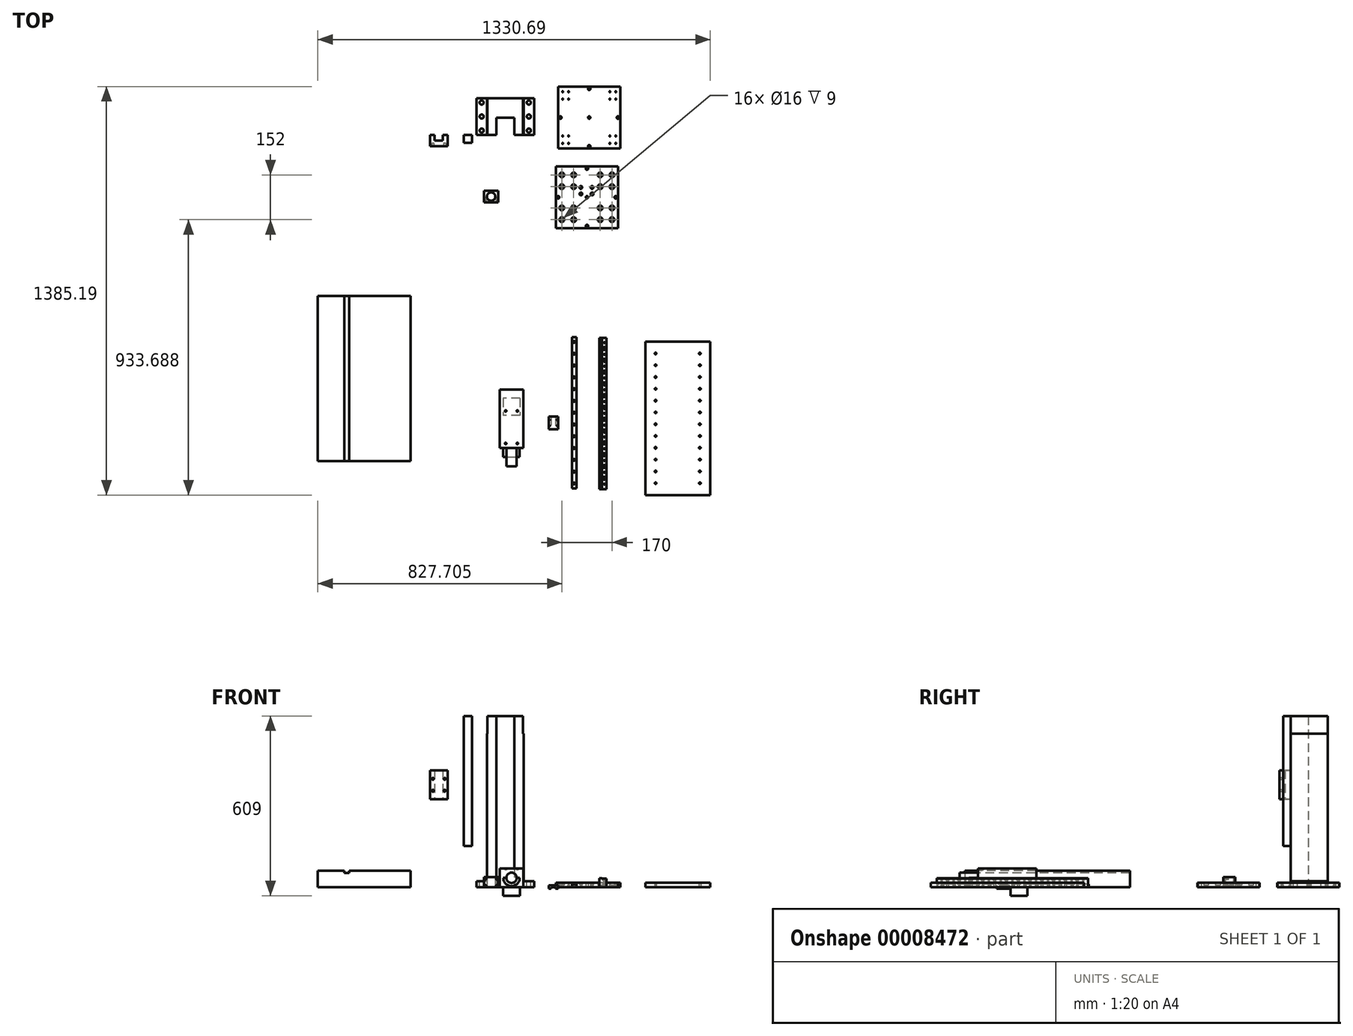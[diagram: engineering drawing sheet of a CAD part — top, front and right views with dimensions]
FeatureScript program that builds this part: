
annotation { "Feature Type Name" : "Feature", "Feature Type Description" : "" }
export const myFeature = defineFeature(function(context is Context, id is Id, definition is map)
    precondition{}
    {
        {
            var Q0;
            Q0=qCreatedBy(makeId("Top.planeOp"),FACE);
            var sketch = newSketch(context, id + "F0", { "sketchPlane" : qUnion([Q0])});
            skLineSegment(sketch, "E0.bottom", {"start": v(-121.15, 80.57) * mm, "end": v(3.85, 80.57) * mm});
            skLineSegment(sketch, "E0.top", {"start": v(-121.15, -44.43) * mm, "end": v(3.85, -44.43) * mm});
            skLineSegment(sketch, "E0.left", {"start": v(-121.15, 80.57) * mm, "end": v(-121.15, -44.43) * mm});
            skLineSegment(sketch, "E0.right", {"start": v(3.85, 80.57) * mm, "end": v(3.85, -44.43) * mm});
            skSolve(sketch);
        }
        {
            var Q0;
            Q0=makeQuery(id+"F0.imprint","IMPRINT",FACE,{"disambiguationData":[TD([[makeQuery(id+"F0.imprint","IMPRINT",EDGE,{"derivedFrom":sQuery(id+"F0.wireOp",EDGE,"E0.bottom")}),-1.0]])]});
            extrude(context, id + "F1", {"entities" : qUnion([Q0]), "depth" : 580 * mm});
        }
        {
            var Q0;
            Q0=makeQuery(id+"F1.opExtrude","SWEPT_FACE",FACE,{"disambiguationData":[OSD([sQuery(id+"F0.wireOp",EDGE,"E0.left")])]});
            var sketch = newSketch(context, id + "F2", { "sketchPlane" : qUnion([Q0])});
            skLineSegment(sketch, "E1.bottom", {"start": v(-80.57, 0) * mm, "end": v(44.43, 0) * mm});
            skLineSegment(sketch, "E1.top", {"start": v(-80.57, 20) * mm, "end": v(44.43, 20) * mm});
            skLineSegment(sketch, "E1.left", {"start": v(-80.57, 0) * mm, "end": v(-80.57, 20) * mm});
            skLineSegment(sketch, "E1.right", {"start": v(44.43, 0) * mm, "end": v(44.43, 20) * mm});
            skSolve(sketch);
        }
        {
            var Q0;
            Q0=makeQuery(id+"F2.imprint","IMPRINT",FACE,{"disambiguationData":[TD([[makeQuery(id+"F2.imprint","IMPRINT",EDGE,{"derivedFrom":sQuery(id+"F2.wireOp",EDGE,"E1.bottom")}),1.0]])]});
            extrude(context, id + "F3", {"entities" : qUnion([Q0]), "operationType" : NewBodyOperationType.ADD, "depth" : 35 * mm});
        }
        {
            var Q0;
            Q0=makeQuery(id+"F1.opExtrude","SWEPT_FACE",FACE,{"disambiguationData":[OSD([sQuery(id+"F0.wireOp",EDGE,"E0.right")])]});
            var sketch = newSketch(context, id + "F4", { "sketchPlane" : qUnion([Q0])});
            skLineSegment(sketch, "E2.bottom", {"start": v(-44.43, 0) * mm, "end": v(80.57, 0) * mm});
            skLineSegment(sketch, "E2.top", {"start": v(-44.43, 20) * mm, "end": v(80.57, 20) * mm});
            skLineSegment(sketch, "E2.left", {"start": v(-44.43, 0) * mm, "end": v(-44.43, 20) * mm});
            skLineSegment(sketch, "E2.right", {"start": v(80.57, 0) * mm, "end": v(80.57, 20) * mm});
            skSolve(sketch);
        }
        {
            var Q0;
            Q0=makeQuery(id+"F4.imprint","IMPRINT",FACE,{"disambiguationData":[TD([[makeQuery(id+"F4.imprint","IMPRINT",EDGE,{"derivedFrom":sQuery(id+"F4.wireOp",EDGE,"E2.bottom")}),-1.0]])]});
            extrude(context, id + "F5", {"entities" : qUnion([Q0]), "operationType" : NewBodyOperationType.ADD, "depth" : 35 * mm});
        }
        {
            var Q0;
            Q0=makeQuery(id+"F5.opExtrude","SWEPT_FACE",FACE,{"disambiguationData":[OSD([sQuery(id+"F4.wireOp",EDGE,"E2.top")])]});
            var sketch = newSketch(context, id + "F6", { "sketchPlane" : qUnion([Q0])});
            skCircle(sketch, "E3", {"center": v(21.35, 65.57) * mm, "radius": 7 * mm});
            skCircle(sketch, "E4", {"center": v(21.35, 18.07) * mm, "radius": 7 * mm});
            skCircle(sketch, "E5", {"center": v(21.35, -29.43) * mm, "radius": 7 * mm});
            skPoint(sketch, "E6", {"position": v(38.85, 18.07) * mm});
            skPoint(sketch, "E7", {"position": v(21.35, 80.57) * mm});
            skSolve(sketch);
        }
        {
            var Q0;
            Q0=makeQuery(id+"F6.imprint","IMPRINT",FACE,{"disambiguationData":[TD([[makeQuery(id+"F6.imprint","IMPRINT",EDGE,{"derivedFrom":sQuery(id+"F6.wireOp",EDGE,"E4")}),1.0]])]});
            var Q1;
            Q1=makeQuery(id+"F6.imprint","IMPRINT",FACE,{"disambiguationData":[TD([[makeQuery(id+"F6.imprint","IMPRINT",EDGE,{"derivedFrom":sQuery(id+"F6.wireOp",EDGE,"E5")}),1.0]])]});
            var Q2;
            Q2=makeQuery(id+"F6.imprint","IMPRINT",FACE,{"disambiguationData":[TD([[makeQuery(id+"F6.imprint","IMPRINT",EDGE,{"derivedFrom":sQuery(id+"F6.wireOp",EDGE,"E3")}),1.0]])]});
            extrude(context, id + "F7", {"entities" : qUnion([Q0, Q1, Q2]), "operationType" : NewBodyOperationType.REMOVE, "oppositeDirection" : true, "depth" : 20 * mm});
        }
        {
            var Q0;
            Q0=makeQuery(id+"F3.opExtrude","SWEPT_FACE",FACE,{"disambiguationData":[OSD([sQuery(id+"F2.wireOp",EDGE,"E1.top")])]});
            var sketch = newSketch(context, id + "F8", { "sketchPlane" : qUnion([Q0])});
            skPoint(sketch, "E8", {"position": v(-138.65, 80.57) * mm});
            skPoint(sketch, "E9", {"position": v(-156.15, 18.07) * mm});
            skCircle(sketch, "E10", {"center": v(-138.65, 65.57) * mm, "radius": 7 * mm});
            skCircle(sketch, "E11", {"center": v(-138.65, 18.07) * mm, "radius": 7 * mm});
            skCircle(sketch, "E12", {"center": v(-138.65, -29.43) * mm, "radius": 7 * mm});
            skSolve(sketch);
        }
        {
            var Q0;
            Q0=makeQuery(id+"F8.imprint","IMPRINT",FACE,{"disambiguationData":[TD([[makeQuery(id+"F8.imprint","IMPRINT",EDGE,{"derivedFrom":sQuery(id+"F8.wireOp",EDGE,"E10")}),1.0]])]});
            var Q1;
            Q1=makeQuery(id+"F8.imprint","IMPRINT",FACE,{"disambiguationData":[TD([[makeQuery(id+"F8.imprint","IMPRINT",EDGE,{"derivedFrom":sQuery(id+"F8.wireOp",EDGE,"E11")}),1.0]])]});
            var Q2;
            Q2=makeQuery(id+"F8.imprint","IMPRINT",FACE,{"disambiguationData":[TD([[makeQuery(id+"F8.imprint","IMPRINT",EDGE,{"derivedFrom":sQuery(id+"F8.wireOp",EDGE,"E12")}),1.0]])]});
            extrude(context, id + "F9", {"entities" : qUnion([Q0, Q1, Q2]), "operationType" : NewBodyOperationType.REMOVE, "oppositeDirection" : true, "depth" : 20 * mm});
        }
        {
            var Q0;
            {var subQ2=sQuery(id+"F2.wireOp",EDGE,"E1.top");Q0=makeQuery(id+"F2.imprint","IMPRINT",FACE,{"disambiguationData":[TD([[makeQuery(id+"F2.imprint","IMPRINT",EDGE,{"derivedFrom":subQ2}),1.0]])]});}
            var sketch = newSketch(context, id + "F10", { "sketchPlane" : qUnion([Q0])});
            skLineSegment(sketch, "E13.bottom", {"start": v(44.43, 580) * mm, "end": v(-80.57, 580) * mm});
            skLineSegment(sketch, "E13.top", {"start": v(44.43, 520) * mm, "end": v(-80.57, 520) * mm});
            skLineSegment(sketch, "E13.left", {"start": v(44.43, 580) * mm, "end": v(44.43, 520) * mm});
            skLineSegment(sketch, "E13.right", {"start": v(-80.57, 580) * mm, "end": v(-80.57, 520) * mm});
            skSolve(sketch);
        }
        {
            var Q0;
            Q0=makeQuery(id+"F10.imprint","IMPRINT",FACE,{"disambiguationData":[TD([[makeQuery(id+"F10.imprint","IMPRINT",EDGE,{"derivedFrom":sQuery(id+"F10.wireOp",EDGE,"E13.bottom")}),-1.0]])]});
            extrude(context, id + "F11", {"entities" : qUnion([Q0]), "operationType" : NewBodyOperationType.REMOVE, "oppositeDirection" : true, "depth" : 2 * mm});
        }
        {
            var Q0;
            {var subQ3=sQuery(id+"F4.wireOp",EDGE,"E2.top");Q0=makeQuery(id+"F4.imprint","IMPRINT",FACE,{"disambiguationData":[TD([[makeQuery(id+"F4.imprint","IMPRINT",EDGE,{"derivedFrom":subQ3}),1.0]])]});}
            var sketch = newSketch(context, id + "F12", { "sketchPlane" : qUnion([Q0])});
            skLineSegment(sketch, "E14.bottom", {"start": v(-44.43, 580) * mm, "end": v(80.57, 580) * mm});
            skLineSegment(sketch, "E14.top", {"start": v(-44.43, 520) * mm, "end": v(80.57, 520) * mm});
            skLineSegment(sketch, "E14.left", {"start": v(-44.43, 580) * mm, "end": v(-44.43, 520) * mm});
            skLineSegment(sketch, "E14.right", {"start": v(80.57, 580) * mm, "end": v(80.57, 520) * mm});
            skLineSegment(sketch, "E15", {"start": v(14.57, 580) * mm, "end": v(14.57, 50.87) * mm});
            skSolve(sketch);
        }
        {
            var Q0;
            Q0=makeQuery(id+"F12.imprint","IMPRINT",FACE,{"disambiguationData":[TD([[makeQuery(id+"F12.imprint","IMPRINT",EDGE,{"derivedFrom":sQuery(id+"F12.wireOp",EDGE,"E14.bottom")}),1.0]])]});
            extrude(context, id + "F13", {"entities" : qUnion([Q0]), "operationType" : NewBodyOperationType.REMOVE, "oppositeDirection" : true, "depth" : 2 * mm});
        }
        {
            var Q0;
            Q0=makeQuery(id+"F5.boolean.opBoolean","MERGE",FACE,{"derivedFrom":[makeQuery(id+"F3.boolean.opBoolean","MERGE",FACE,{"derivedFrom":[makeQuery(id+"F1.opExtrude","SWEPT_FACE",FACE,{"disambiguationData":[OSD([sQuery(id+"F0.wireOp",EDGE,"E0.top")])]}),makeQuery(id+"F3.opExtrude","SWEPT_FACE",FACE,{"disambiguationData":[OSD([sQuery(id+"F2.wireOp",EDGE,"E1.right")])]})]}),makeQuery(id+"F5.opExtrude","SWEPT_FACE",FACE,{"disambiguationData":[OSD([sQuery(id+"F4.wireOp",EDGE,"E2.left")])]})]});
            var sketch = newSketch(context, id + "F14", { "sketchPlane" : qUnion([Q0])});
            skPoint(sketch, "E16", {"position": v(-58.65, 580) * mm});
            skLineSegment(sketch, "E17.bottom", {"start": v(-88.9, 580) * mm, "end": v(-28.4, 580) * mm});
            skLineSegment(sketch, "E17.top", {"start": v(-88.9, 0) * mm, "end": v(-28.4, 0) * mm});
            skLineSegment(sketch, "E17.left", {"start": v(-88.9, 580) * mm, "end": v(-88.9, 0) * mm});
            skLineSegment(sketch, "E17.right", {"start": v(-28.4, 580) * mm, "end": v(-28.4, 0) * mm});
            skSolve(sketch);
        }
        {
            var Q0;
            Q0=makeQuery(id+"F14.imprint","IMPRINT",FACE,{"disambiguationData":[TD([[makeQuery(id+"F14.imprint","IMPRINT",EDGE,{"derivedFrom":sQuery(id+"F14.wireOp",EDGE,"E17.bottom")}),-1.0]])]});
            extrude(context, id + "F15", {"entities" : qUnion([Q0]), "operationType" : NewBodyOperationType.REMOVE, "oppositeDirection" : true, "depth" : 59 * mm});
        }
        {
            var Q0;
            Q0=makeQuery(id+"F5.boolean.opBoolean","MERGE",FACE,{"derivedFrom":[makeQuery(id+"F3.boolean.opBoolean","MERGE",FACE,{"derivedFrom":[makeQuery(id+"F1.opExtrude","SWEPT_FACE",FACE,{"disambiguationData":[OSD([sQuery(id+"F0.wireOp",EDGE,"E0.top")])]}),makeQuery(id+"F3.opExtrude","SWEPT_FACE",FACE,{"disambiguationData":[OSD([sQuery(id+"F2.wireOp",EDGE,"E1.right")])]})]}),makeQuery(id+"F5.opExtrude","SWEPT_FACE",FACE,{"disambiguationData":[OSD([sQuery(id+"F4.wireOp",EDGE,"E2.left")])]})]});
            var sketch = newSketch(context, id + "F16", { "sketchPlane" : qUnion([Q0])});
            skLineSegment(sketch, "E18.bottom", {"start": v(-199.32, 580) * mm, "end": v(-171.32, 580) * mm});
            skLineSegment(sketch, "E18.top", {"start": v(-199.32, 140) * mm, "end": v(-171.32, 140) * mm});
            skLineSegment(sketch, "E18.left", {"start": v(-199.32, 580) * mm, "end": v(-199.32, 140) * mm});
            skLineSegment(sketch, "E18.right", {"start": v(-171.32, 580) * mm, "end": v(-171.32, 140) * mm});
            skPoint(sketch, "E19", {"position": v(-185.32, 580) * mm});
            skPoint(sketch, "E20", {"position": v(-122.53, 0) * mm});
            skLineSegment(sketch, "E21.bottom", {"start": v(-314.15, 396.2) * mm, "end": v(-254.15, 396.2) * mm});
            skLineSegment(sketch, "E21.top", {"start": v(-314.15, 298.2) * mm, "end": v(-254.15, 298.2) * mm});
            skLineSegment(sketch, "E21.left", {"start": v(-314.15, 396.2) * mm, "end": v(-314.15, 298.2) * mm});
            skLineSegment(sketch, "E21.right", {"start": v(-254.15, 396.2) * mm, "end": v(-254.15, 298.2) * mm});
            skPoint(sketch, "E22", {"position": v(-284.15, 298.2) * mm});
            skSolve(sketch);
        }
        {
            var Q0;
            Q0=makeQuery(id+"F16.imprint","IMPRINT",FACE,{"disambiguationData":[TD([[makeQuery(id+"F16.imprint","IMPRINT",EDGE,{"derivedFrom":sQuery(id+"F16.wireOp",EDGE,"E18.bottom")}),-1.0]])]});
            extrude(context, id + "F17", {"entities" : qUnion([Q0]), "depth" : 26 * mm});
        }
        {
            var Q0;
            Q0=makeQuery(id+"F16.imprint","IMPRINT",FACE,{"disambiguationData":[TD([[makeQuery(id+"F16.imprint","IMPRINT",EDGE,{"derivedFrom":sQuery(id+"F16.wireOp",EDGE,"E21.bottom")}),-1.0]])]});
            extrude(context, id + "F18", {"entities" : qUnion([Q0]), "depth" : 38 * mm});
        }
        {
            var Q0;
            Q0=makeQuery(id+"F18.opExtrude","SWEPT_FACE",FACE,{"disambiguationData":[OSD([sQuery(id+"F16.wireOp",EDGE,"E21.top")])]});
            var sketch = newSketch(context, id + "F19", { "sketchPlane" : qUnion([Q0])});
            skLineSegment(sketch, "E23.bottom", {"start": v(-298.15, 44.43) * mm, "end": v(-270.15, 44.43) * mm});
            skLineSegment(sketch, "E23.top", {"start": v(-298.15, 63.43) * mm, "end": v(-270.15, 63.43) * mm});
            skLineSegment(sketch, "E23.left", {"start": v(-298.15, 44.43) * mm, "end": v(-298.15, 63.43) * mm});
            skLineSegment(sketch, "E23.right", {"start": v(-270.15, 44.43) * mm, "end": v(-270.15, 63.43) * mm});
            skPoint(sketch, "E24", {"position": v(-284.15, 44.43) * mm});
            skSolve(sketch);
        }
        {
            var Q0;
            Q0=makeQuery(id+"F19.imprint","IMPRINT",FACE,{"disambiguationData":[TD([[makeQuery(id+"F19.imprint","IMPRINT",EDGE,{"derivedFrom":sQuery(id+"F19.wireOp",EDGE,"E23.bottom")}),1.0]])]});
            extrude(context, id + "F20", {"entities" : qUnion([Q0]), "operationType" : NewBodyOperationType.REMOVE, "oppositeDirection" : true, "depth" : 98 * mm});
        }
        {
            var Q0;
            Q0=makeQuery(id+"F18.opExtrude","CAP_FACE",FACE,{"disambiguationData":[OSD([sQuery(id+"F16.wireOp",EDGE,"E21.bottom"),sQuery(id+"F16.wireOp",EDGE,"E21.top"),sQuery(id+"F16.wireOp",EDGE,"E21.left"),sQuery(id+"F16.wireOp",EDGE,"E21.right")])],"isStart":false});
            var sketch = newSketch(context, id + "F21", { "sketchPlane" : qUnion([Q0])});
            skCircle(sketch, "E25", {"center": v(-304.15, 367.2) * mm, "radius": 3.35 * mm});
            skCircle(sketch, "E26", {"center": v(-304.15, 327.2) * mm, "radius": 3.35 * mm});
            skCircle(sketch, "E27", {"center": v(-264.15, 367.2) * mm, "radius": 3.35 * mm});
            skCircle(sketch, "E28", {"center": v(-264.15, 327.2) * mm, "radius": 3.35 * mm});
            skPoint(sketch, "E29", {"position": v(-284.15, 396.2) * mm});
            skLineSegment(sketch, "E30", {"start": v(-284.15, 396.2) * mm, "end": v(-284.15, 298.2) * mm});
            skPoint(sketch, "E31", {"position": v(-284.15, 347.2) * mm});
            skSolve(sketch);
        }
        {
            var Q0;
            Q0=makeQuery(id+"F21.imprint","IMPRINT",FACE,{"disambiguationData":[TD([[makeQuery(id+"F21.imprint","IMPRINT",EDGE,{"derivedFrom":sQuery(id+"F21.wireOp",EDGE,"E25")}),1.0]])]});
            var Q1;
            Q1=makeQuery(id+"F21.imprint","IMPRINT",FACE,{"disambiguationData":[TD([[makeQuery(id+"F21.imprint","IMPRINT",EDGE,{"derivedFrom":sQuery(id+"F21.wireOp",EDGE,"E26")}),1.0]])]});
            var Q2;
            Q2=makeQuery(id+"F21.imprint","IMPRINT",FACE,{"disambiguationData":[TD([[makeQuery(id+"F21.imprint","IMPRINT",EDGE,{"derivedFrom":sQuery(id+"F21.wireOp",EDGE,"E27")}),1.0]])]});
            var Q3;
            Q3=makeQuery(id+"F21.imprint","IMPRINT",FACE,{"disambiguationData":[TD([[makeQuery(id+"F21.imprint","IMPRINT",EDGE,{"derivedFrom":sQuery(id+"F21.wireOp",EDGE,"E28")}),1.0]])]});
            extrude(context, id + "F22", {"entities" : qUnion([Q0, Q1, Q2, Q3]), "operationType" : NewBodyOperationType.REMOVE, "oppositeDirection" : true, "depth" : 10 * mm});
        }
        {
            var Q0;
            Q0=qCreatedBy(makeId("Top.planeOp"),FACE);
            var sketch = newSketch(context, id + "F23", { "sketchPlane" : qUnion([Q0])});
            skLineSegment(sketch, "E32.bottom", {"start": v(120.9, 119.72) * mm, "end": v(330.9, 119.72) * mm});
            skLineSegment(sketch, "E32.top", {"start": v(120.9, -90.28) * mm, "end": v(330.9, -90.28) * mm});
            skLineSegment(sketch, "E32.left", {"start": v(120.9, 119.72) * mm, "end": v(120.9, -90.28) * mm});
            skLineSegment(sketch, "E32.right", {"start": v(330.9, 119.72) * mm, "end": v(330.9, -90.28) * mm});
            skCircle(sketch, "E33", {"center": v(225.9, 14.72) * mm, "radius": 4 * mm});
            skCircle(sketch, "E34", {"center": v(323.4, 14.72) * mm, "radius": 4.2 * mm});
            skCircle(sketch, "E35", {"center": v(225.9, 112.22) * mm, "radius": 4.2 * mm});
            skCircle(sketch, "E36", {"center": v(128.4, 14.72) * mm, "radius": 4.2 * mm});
            skCircle(sketch, "E37", {"center": v(225.9, -82.78) * mm, "radius": 4.2 * mm});
            skLineSegment(sketch, "E38.bottom", {"start": v(113.2, -150.78) * mm, "end": v(323.2, -150.78) * mm});
            skLineSegment(sketch, "E38.top", {"start": v(113.2, -360.78) * mm, "end": v(323.2, -360.78) * mm});
            skLineSegment(sketch, "E38.left", {"start": v(113.2, -150.78) * mm, "end": v(113.2, -360.78) * mm});
            skLineSegment(sketch, "E38.right", {"start": v(323.2, -150.78) * mm, "end": v(323.2, -360.78) * mm});
            skCircle(sketch, "E39", {"center": v(218.2, -255.78) * mm, "radius": 4 * mm});
            skCircle(sketch, "E40", {"center": v(218.2, -158.28) * mm, "radius": 4.2 * mm});
            skCircle(sketch, "E41", {"center": v(120.7, -255.78) * mm, "radius": 4.2 * mm});
            skCircle(sketch, "E42", {"center": v(315.7, -255.78) * mm, "radius": 4.2 * mm});
            skCircle(sketch, "E43", {"center": v(218.2, -353.28) * mm, "radius": 4.2 * mm});
            skLineSegment(sketch, "E44.bottom", {"start": v(-694.5, -590.16) * mm, "end": v(-379.5, -590.16) * mm});
            skLineSegment(sketch, "E44.top", {"start": v(-694.5, -1150.16) * mm, "end": v(-379.5, -1150.16) * mm});
            skLineSegment(sketch, "E44.left", {"start": v(-694.5, -590.16) * mm, "end": v(-694.5, -1150.16) * mm});
            skLineSegment(sketch, "E44.right", {"start": v(-379.5, -590.16) * mm, "end": v(-379.5, -1150.16) * mm});
            skLineSegment(sketch, "E45.bottom", {"start": v(-130.67, -233.25) * mm, "end": v(-82.67, -233.25) * mm});
            skLineSegment(sketch, "E45.top", {"start": v(-130.67, -273.25) * mm, "end": v(-82.67, -273.25) * mm});
            skLineSegment(sketch, "E45.left", {"start": v(-130.67, -233.25) * mm, "end": v(-130.67, -273.25) * mm});
            skLineSegment(sketch, "E45.right", {"start": v(-82.67, -233.25) * mm, "end": v(-82.67, -273.25) * mm});
            skPoint(sketch, "E46", {"position": v(-106.67, -253.25) * mm});
            skCircle(sketch, "E47", {"center": v(-106.67, -253.25) * mm, "radius": 14 * mm});
            skCircle(sketch, "E48", {"center": v(303.2, -179.78) * mm, "radius": 4.5 * mm});
            skCircle(sketch, "E49", {"center": v(263.2, -179.78) * mm, "radius": 4.5 * mm});
            skCircle(sketch, "E50", {"center": v(263.2, -219.78) * mm, "radius": 4.5 * mm});
            skCircle(sketch, "E51", {"center": v(303.2, -219.78) * mm, "radius": 4.5 * mm});
            skCircle(sketch, "E52", {"center": v(303.2, -331.78) * mm, "radius": 4.5 * mm});
            skCircle(sketch, "E53", {"center": v(303.2, -291.78) * mm, "radius": 4.5 * mm});
            skCircle(sketch, "E54", {"center": v(263.2, -291.78) * mm, "radius": 4.5 * mm});
            skCircle(sketch, "E55", {"center": v(263.2, -331.78) * mm, "radius": 4.5 * mm});
            skCircle(sketch, "E56", {"center": v(173.2, -219.78) * mm, "radius": 4.5 * mm});
            skCircle(sketch, "E57", {"center": v(173.2, -179.78) * mm, "radius": 4.5 * mm});
            skCircle(sketch, "E58", {"center": v(133.2, -179.78) * mm, "radius": 4.5 * mm});
            skCircle(sketch, "E59", {"center": v(133.2, -219.78) * mm, "radius": 4.5 * mm});
            skCircle(sketch, "E60", {"center": v(173.2, -331.78) * mm, "radius": 4.5 * mm});
            skCircle(sketch, "E61", {"center": v(173.2, -291.78) * mm, "radius": 4.5 * mm});
            skCircle(sketch, "E62", {"center": v(133.2, -291.78) * mm, "radius": 4.5 * mm});
            skCircle(sketch, "E63", {"center": v(133.2, -331.78) * mm, "radius": 4.5 * mm});
            skCircle(sketch, "E64", {"center": v(263.2, -179.78) * mm, "radius": 8 * mm});
            skCircle(sketch, "E65", {"center": v(303.2, -179.78) * mm, "radius": 8 * mm});
            skCircle(sketch, "E66", {"center": v(263.2, -219.78) * mm, "radius": 8 * mm});
            skCircle(sketch, "E67", {"center": v(303.2, -219.78) * mm, "radius": 8 * mm});
            skCircle(sketch, "E68", {"center": v(263.2, -291.78) * mm, "radius": 8 * mm});
            skCircle(sketch, "E69", {"center": v(303.2, -291.78) * mm, "radius": 8 * mm});
            skCircle(sketch, "E70", {"center": v(263.2, -331.78) * mm, "radius": 8 * mm});
            skCircle(sketch, "E71", {"center": v(303.2, -331.78) * mm, "radius": 8 * mm});
            skCircle(sketch, "E72", {"center": v(173.2, -179.78) * mm, "radius": 8 * mm});
            skCircle(sketch, "E73", {"center": v(133.2, -179.78) * mm, "radius": 8 * mm});
            skCircle(sketch, "E74", {"center": v(133.2, -219.78) * mm, "radius": 8 * mm});
            skCircle(sketch, "E75", {"center": v(173.2, -219.78) * mm, "radius": 8 * mm});
            skCircle(sketch, "E76", {"center": v(133.2, -291.78) * mm, "radius": 8 * mm});
            skCircle(sketch, "E77", {"center": v(173.2, -291.78) * mm, "radius": 8 * mm});
            skCircle(sketch, "E78", {"center": v(133.2, -331.78) * mm, "radius": 8 * mm});
            skCircle(sketch, "E79", {"center": v(173.2, -331.78) * mm, "radius": 8 * mm});
            skCircle(sketch, "E80", {"center": v(197.7, -222.28) * mm, "radius": 2.65 * mm});
            skCircle(sketch, "E81", {"center": v(235.7, -222.28) * mm, "radius": 2.65 * mm});
            skCircle(sketch, "E82", {"center": v(197.7, -244.28) * mm, "radius": 2.65 * mm});
            skCircle(sketch, "E83", {"center": v(235.7, -244.28) * mm, "radius": 2.65 * mm});
            skCircle(sketch, "E84", {"center": v(197.7, -222.28) * mm, "radius": 4.75 * mm});
            skCircle(sketch, "E85", {"center": v(235.7, -222.28) * mm, "radius": 4.75 * mm});
            skCircle(sketch, "E86", {"center": v(197.7, -244.28) * mm, "radius": 4.75 * mm});
            skCircle(sketch, "E87", {"center": v(235.7, -244.28) * mm, "radius": 4.75 * mm});
            skLineSegment(sketch, "E88.bottom", {"start": v(-77.51, -907.41) * mm, "end": v(2.49, -907.41) * mm});
            skLineSegment(sketch, "E88.top", {"start": v(-77.51, -1105.61) * mm, "end": v(2.49, -1105.61) * mm});
            skLineSegment(sketch, "E88.left", {"start": v(-77.51, -907.41) * mm, "end": v(-77.51, -1105.61) * mm});
            skLineSegment(sketch, "E88.right", {"start": v(2.49, -907.41) * mm, "end": v(2.49, -1105.61) * mm});
            skCircle(sketch, "E89", {"center": v(-57.51, -1090.61) * mm, "radius": 2.68 * mm});
            skCircle(sketch, "E90", {"center": v(-17.51, -1090.61) * mm, "radius": 2.68 * mm});
            skCircle(sketch, "E91", {"center": v(-57.51, -980.61) * mm, "radius": 2.68 * mm});
            skCircle(sketch, "E92", {"center": v(-17.51, -980.61) * mm, "radius": 2.68 * mm});
            skLineSegment(sketch, "E93.bottom", {"start": v(88.31, -999.03) * mm, "end": v(120.31, -999.03) * mm});
            skLineSegment(sketch, "E93.top", {"start": v(88.31, -1042.03) * mm, "end": v(120.31, -1042.03) * mm});
            skLineSegment(sketch, "E93.left", {"start": v(88.31, -999.03) * mm, "end": v(88.31, -1042.03) * mm});
            skLineSegment(sketch, "E93.right", {"start": v(120.31, -999.03) * mm, "end": v(120.31, -1042.03) * mm});
            skLineSegment(sketch, "E94.bottom", {"start": v(167.32, -729.85) * mm, "end": v(182.32, -729.85) * mm});
            skLineSegment(sketch, "E94.top", {"start": v(167.32, -1242.85) * mm, "end": v(182.32, -1242.85) * mm});
            skLineSegment(sketch, "E94.left", {"start": v(167.32, -729.85) * mm, "end": v(167.32, -1242.85) * mm});
            skLineSegment(sketch, "E94.right", {"start": v(182.32, -729.85) * mm, "end": v(182.32, -1242.85) * mm});
            skCircle(sketch, "E95", {"center": v(174.82, -746.35) * mm, "radius": 1.75 * mm});
            skCircle(sketch, "E96", {"center": v(174.82, -786.35) * mm, "radius": 1.75 * mm});
            skCircle(sketch, "E97", {"center": v(174.82, -826.35) * mm, "radius": 1.75 * mm});
            skCircle(sketch, "E98", {"center": v(174.82, -866.35) * mm, "radius": 1.75 * mm});
            skCircle(sketch, "E99", {"center": v(174.82, -906.35) * mm, "radius": 1.75 * mm});
            skCircle(sketch, "E100", {"center": v(174.82, -946.35) * mm, "radius": 1.75 * mm});
            skCircle(sketch, "E101", {"center": v(174.82, -986.35) * mm, "radius": 1.75 * mm});
            skCircle(sketch, "E102", {"center": v(174.82, -1026.35) * mm, "radius": 1.75 * mm});
            skCircle(sketch, "E103", {"center": v(174.82, -1066.35) * mm, "radius": 1.75 * mm});
            skCircle(sketch, "E104", {"center": v(174.82, -1106.35) * mm, "radius": 1.75 * mm});
            skCircle(sketch, "E105", {"center": v(174.82, -1146.35) * mm, "radius": 1.75 * mm});
            skCircle(sketch, "E106", {"center": v(174.82, -1186.35) * mm, "radius": 1.75 * mm});
            skCircle(sketch, "E107", {"center": v(174.82, -1226.35) * mm, "radius": 1.75 * mm});
            skPoint(sketch, "E108", {"position": v(174.82, -729.85) * mm});
            skPoint(sketch, "E109", {"position": v(277.23, -732.27) * mm});
            skLineSegment(sketch, "E110.right", {"start": v(284.73, -732.27) * mm, "end": v(284.73, -1245.27) * mm});
            skLineSegment(sketch, "E110.left", {"start": v(269.73, -732.27) * mm, "end": v(269.73, -1245.27) * mm});
            skCircle(sketch, "E111", {"center": v(277.23, -948.77) * mm, "radius": 1.75 * mm});
            skCircle(sketch, "E112", {"center": v(277.23, -1228.77) * mm, "radius": 1.75 * mm});
            skCircle(sketch, "E113", {"center": v(277.23, -1068.77) * mm, "radius": 1.75 * mm});
            skCircle(sketch, "E114", {"center": v(277.23, -1108.77) * mm, "radius": 1.75 * mm});
            skCircle(sketch, "E115", {"center": v(277.23, -1148.77) * mm, "radius": 1.75 * mm});
            skCircle(sketch, "E116", {"center": v(277.23, -988.77) * mm, "radius": 1.75 * mm});
            skCircle(sketch, "E117", {"center": v(277.23, -908.77) * mm, "radius": 1.75 * mm});
            skCircle(sketch, "E118", {"center": v(277.23, -788.77) * mm, "radius": 1.75 * mm});
            skLineSegment(sketch, "E110.top", {"start": v(269.73, -1245.27) * mm, "end": v(284.73, -1245.27) * mm});
            skCircle(sketch, "E119", {"center": v(277.23, -868.77) * mm, "radius": 1.75 * mm});
            skCircle(sketch, "E120", {"center": v(277.23, -1188.77) * mm, "radius": 1.75 * mm});
            skCircle(sketch, "E121", {"center": v(277.23, -1028.77) * mm, "radius": 1.75 * mm});
            skCircle(sketch, "E122", {"center": v(277.23, -748.77) * mm, "radius": 1.75 * mm});
            skCircle(sketch, "E123", {"center": v(277.23, -828.77) * mm, "radius": 1.75 * mm});
            skLineSegment(sketch, "E110.bottom", {"start": v(269.73, -732.27) * mm, "end": v(284.73, -732.27) * mm});
            skLineSegment(sketch, "E124.bottom", {"start": v(269.73, -732.27) * mm, "end": v(260.23, -732.27) * mm});
            skLineSegment(sketch, "E124.top", {"start": v(269.73, -1245.27) * mm, "end": v(260.23, -1245.27) * mm});
            skLineSegment(sketch, "E124.right", {"start": v(260.23, -732.27) * mm, "end": v(260.23, -1245.27) * mm});
            skCircle(sketch, "E125", {"center": v(277.23, -1208.77) * mm, "radius": 2.8 * mm});
            skCircle(sketch, "E126", {"center": v(277.23, -1168.77) * mm, "radius": 2.8 * mm});
            skCircle(sketch, "E127", {"center": v(277.23, -1128.77) * mm, "radius": 2.8 * mm});
            skCircle(sketch, "E128", {"center": v(277.23, -1088.77) * mm, "radius": 2.8 * mm});
            skCircle(sketch, "E129", {"center": v(277.23, -1048.77) * mm, "radius": 2.8 * mm});
            skCircle(sketch, "E130", {"center": v(277.23, -1008.77) * mm, "radius": 2.8 * mm});
            skCircle(sketch, "E131", {"center": v(277.23, -968.77) * mm, "radius": 2.8 * mm});
            skCircle(sketch, "E132", {"center": v(277.23, -928.77) * mm, "radius": 2.8 * mm});
            skCircle(sketch, "E133", {"center": v(277.23, -888.77) * mm, "radius": 2.8 * mm});
            skCircle(sketch, "E134", {"center": v(277.23, -848.77) * mm, "radius": 2.8 * mm});
            skCircle(sketch, "E135", {"center": v(277.23, -808.77) * mm, "radius": 2.8 * mm});
            skCircle(sketch, "E136", {"center": v(277.23, -768.77) * mm, "radius": 2.8 * mm});
            skLineSegment(sketch, "E137.bottom", {"start": v(416.18, -745.47) * mm, "end": v(636.18, -745.47) * mm});
            skLineSegment(sketch, "E137.top", {"start": v(416.18, -1265.47) * mm, "end": v(636.18, -1265.47) * mm});
            skLineSegment(sketch, "E137.left", {"start": v(416.18, -745.47) * mm, "end": v(416.18, -1265.47) * mm});
            skLineSegment(sketch, "E137.right", {"start": v(636.18, -745.47) * mm, "end": v(636.18, -1265.47) * mm});
            skCircle(sketch, "E138", {"center": v(451.18, -905.47) * mm, "radius": 2.8 * mm});
            skCircle(sketch, "E139", {"center": v(451.18, -865.47) * mm, "radius": 2.8 * mm});
            skCircle(sketch, "E140", {"center": v(451.18, -825.47) * mm, "radius": 2.8 * mm});
            skCircle(sketch, "E141", {"center": v(451.18, -785.47) * mm, "radius": 2.8 * mm});
            skCircle(sketch, "E142", {"center": v(451.18, -1065.47) * mm, "radius": 2.8 * mm});
            skCircle(sketch, "E143", {"center": v(451.18, -1105.47) * mm, "radius": 2.8 * mm});
            skCircle(sketch, "E144", {"center": v(451.18, -1145.47) * mm, "radius": 2.8 * mm});
            skCircle(sketch, "E145", {"center": v(451.18, -1185.47) * mm, "radius": 2.8 * mm});
            skCircle(sketch, "E146", {"center": v(451.18, -1225.47) * mm, "radius": 2.8 * mm});
            skCircle(sketch, "E147", {"center": v(451.18, -945.47) * mm, "radius": 2.8 * mm});
            skCircle(sketch, "E148", {"center": v(451.18, -985.47) * mm, "radius": 2.8 * mm});
            skCircle(sketch, "E149", {"center": v(451.18, -1025.47) * mm, "radius": 2.8 * mm});
            skCircle(sketch, "E150", {"center": v(601.18, -905.47) * mm, "radius": 2.8 * mm});
            skCircle(sketch, "E151", {"center": v(601.18, -865.47) * mm, "radius": 2.8 * mm});
            skCircle(sketch, "E152", {"center": v(601.18, -825.47) * mm, "radius": 2.8 * mm});
            skCircle(sketch, "E153", {"center": v(601.18, -785.47) * mm, "radius": 2.8 * mm});
            skCircle(sketch, "E154", {"center": v(601.18, -1065.47) * mm, "radius": 2.8 * mm});
            skCircle(sketch, "E155", {"center": v(601.18, -1105.47) * mm, "radius": 2.8 * mm});
            skCircle(sketch, "E156", {"center": v(601.18, -1145.47) * mm, "radius": 2.8 * mm});
            skCircle(sketch, "E157", {"center": v(601.18, -1185.47) * mm, "radius": 2.8 * mm});
            skCircle(sketch, "E158", {"center": v(601.18, -1225.47) * mm, "radius": 2.8 * mm});
            skCircle(sketch, "E159", {"center": v(601.18, -945.47) * mm, "radius": 2.8 * mm});
            skCircle(sketch, "E160", {"center": v(601.18, -985.47) * mm, "radius": 2.8 * mm});
            skCircle(sketch, "E161", {"center": v(601.18, -1025.47) * mm, "radius": 2.8 * mm});
            skPoint(sketch, "E162", {"position": v(526.18, -745.47) * mm});
            skCircle(sketch, "E163", {"center": v(135.9, 102.22) * mm, "radius": 1.6 * mm});
            skCircle(sketch, "E164", {"center": v(155.9, 102.22) * mm, "radius": 1.6 * mm});
            skCircle(sketch, "E165", {"center": v(135.9, 77.22) * mm, "radius": 1.6 * mm});
            skCircle(sketch, "E166", {"center": v(155.9, 77.22) * mm, "radius": 1.6 * mm});
            skCircle(sketch, "E167", {"center": v(155.9, 102.22) * mm, "radius": 3 * mm});
            skCircle(sketch, "E168", {"center": v(155.9, 77.22) * mm, "radius": 3 * mm});
            skCircle(sketch, "E169", {"center": v(135.9, 102.22) * mm, "radius": 3 * mm});
            skCircle(sketch, "E170", {"center": v(135.9, 77.22) * mm, "radius": 3 * mm});
            skCircle(sketch, "E171.1.0.0", {"center": v(295.9, 77.22) * mm, "radius": 1.6 * mm});
            skCircle(sketch, "E171.1.0.1", {"center": v(295.9, 102.22) * mm, "radius": 1.6 * mm});
            skCircle(sketch, "E171.1.0.2", {"center": v(295.9, 77.22) * mm, "radius": 3 * mm});
            skCircle(sketch, "E171.1.0.3", {"center": v(315.9, 102.22) * mm, "radius": 1.6 * mm});
            skCircle(sketch, "E171.1.0.4", {"center": v(315.9, 77.22) * mm, "radius": 3 * mm});
            skCircle(sketch, "E171.1.0.5", {"center": v(315.9, 77.22) * mm, "radius": 1.6 * mm});
            skCircle(sketch, "E171.1.0.6", {"center": v(315.9, 102.22) * mm, "radius": 3 * mm});
            skCircle(sketch, "E171.1.0.7", {"center": v(295.9, 102.22) * mm, "radius": 3 * mm});
            skLineSegment(sketch, "E171.direction1", {"start": v(155.9, 77.22) * mm, "end": v(315.9, 77.22) * mm, "construction": true});
            skLineSegment(sketch, "E172.1.0.0", {"start": v(155.9, -72.78) * mm, "end": v(315.9, -72.78) * mm, "construction": true});
            skCircle(sketch, "E172.1.0.1", {"center": v(135.9, -47.78) * mm, "radius": 1.6 * mm});
            skCircle(sketch, "E172.1.0.2", {"center": v(155.9, -47.78) * mm, "radius": 1.6 * mm});
            skCircle(sketch, "E172.1.0.3", {"center": v(315.9, -47.78) * mm, "radius": 3 * mm});
            skCircle(sketch, "E172.1.0.4", {"center": v(295.9, -72.78) * mm, "radius": 3 * mm});
            skCircle(sketch, "E172.1.0.5", {"center": v(295.9, -72.78) * mm, "radius": 1.6 * mm});
            skCircle(sketch, "E172.1.0.6", {"center": v(135.9, -72.78) * mm, "radius": 3 * mm});
            skCircle(sketch, "E172.1.0.7", {"center": v(315.9, -47.78) * mm, "radius": 1.6 * mm});
            skCircle(sketch, "E172.1.0.8", {"center": v(135.9, -47.78) * mm, "radius": 3 * mm});
            skCircle(sketch, "E172.1.0.9", {"center": v(135.9, -72.78) * mm, "radius": 1.6 * mm});
            skCircle(sketch, "E172.1.0.10", {"center": v(155.9, -47.78) * mm, "radius": 3 * mm});
            skCircle(sketch, "E172.1.0.11", {"center": v(315.9, -72.78) * mm, "radius": 3 * mm});
            skCircle(sketch, "E172.1.0.12", {"center": v(295.9, -47.78) * mm, "radius": 3 * mm});
            skCircle(sketch, "E172.1.0.13", {"center": v(295.9, -47.78) * mm, "radius": 1.6 * mm});
            skCircle(sketch, "E172.1.0.14", {"center": v(155.9, -72.78) * mm, "radius": 1.6 * mm});
            skCircle(sketch, "E172.1.0.15", {"center": v(315.9, -72.78) * mm, "radius": 1.6 * mm});
            skCircle(sketch, "E172.1.0.16", {"center": v(155.9, -72.78) * mm, "radius": 3 * mm});
            skLineSegment(sketch, "E172.direction1", {"start": v(155.9, 77.22) * mm, "end": v(155.9, -72.78) * mm, "construction": true});
            skSolve(sketch);
        }
        {
            var Q0;
            Q0=makeQuery(id+"F23.imprint","IMPRINT",FACE,{"disambiguationData":[TD([[makeQuery(id+"F23.imprint","IMPRINT",EDGE,{"derivedFrom":sQuery(id+"F23.wireOp",EDGE,"E32.bottom")}),-1.0]])]});
            extrude(context, id + "F24", {"entities" : qUnion([Q0]), "depth" : 15 * mm});
        }
        {
            var Q0;
            Q0=makeQuery(id+"F23.imprint","IMPRINT",FACE,{"disambiguationData":[TD([[makeQuery(id+"F23.imprint","IMPRINT",EDGE,{"derivedFrom":sQuery(id+"F23.wireOp",EDGE,"E38.bottom")}),-1.0]])]});
            extrude(context, id + "F25", {"entities" : qUnion([Q0]), "depth" : 15 * mm});
        }
        {
            var Q0;
            Q0=makeQuery(id+"F23.imprint","IMPRINT",FACE,{"disambiguationData":[TD([[makeQuery(id+"F23.imprint","IMPRINT",EDGE,{"derivedFrom":sQuery(id+"F23.wireOp",EDGE,"E44.bottom")}),-1.0]])]});
            extrude(context, id + "F27", {"entities" : qUnion([Q0]), "depth" : 55 * mm});
        }
        {
            var Q0;
            Q0=makeQuery(id+"F23.imprint","IMPRINT",FACE,{"disambiguationData":[TD([[makeQuery(id+"F23.imprint","IMPRINT",EDGE,{"derivedFrom":sQuery(id+"F23.wireOp",EDGE,"E45.bottom")}),-1.0]])]});
            extrude(context, id + "F28", {"entities" : qUnion([Q0]), "depth" : 34 * mm});
        }
        {
            var Q0;
            Q0=makeQuery(id+"F27.opExtrude","SWEPT_FACE",FACE,{"disambiguationData":[OSD([sQuery(id+"F23.wireOp",EDGE,"E44.top")])]});
            var sketch = newSketch(context, id + "F29", { "sketchPlane" : qUnion([Q0])});
            skLineSegment(sketch, "E173.bottom", {"start": v(-604.5, 55) * mm, "end": v(-588.5, 55) * mm});
            skLineSegment(sketch, "E173.top", {"start": v(-604.5, 47.5) * mm, "end": v(-588.5, 47.5) * mm});
            skLineSegment(sketch, "E173.left", {"start": v(-604.5, 55) * mm, "end": v(-604.5, 47.5) * mm});
            skLineSegment(sketch, "E173.right", {"start": v(-588.5, 55) * mm, "end": v(-588.5, 47.5) * mm});
            skSolve(sketch);
        }
        {
            var Q0;
            Q0=makeQuery(id+"F29.imprint","IMPRINT",FACE,{"disambiguationData":[TD([[makeQuery(id+"F29.imprint","IMPRINT",EDGE,{"derivedFrom":sQuery(id+"F29.wireOp",EDGE,"E173.bottom")}),-1.0]])]});
            extrude(context, id + "F30", {"entities" : qUnion([Q0]), "operationType" : NewBodyOperationType.REMOVE, "oppositeDirection" : true, "depth" : 560 * mm});
        }
        {
            var Q0;
            Q0=makeQuery(id+"F23.imprint","IMPRINT",FACE,{"disambiguationData":[TD([[makeQuery(id+"F23.imprint","IMPRINT",EDGE,{"derivedFrom":sQuery(id+"F23.wireOp",EDGE,"E55")}),-1.0]])]});
            var Q1;
            Q1=makeQuery(id+"F23.imprint","IMPRINT",FACE,{"disambiguationData":[TD([[makeQuery(id+"F23.imprint","IMPRINT",EDGE,{"derivedFrom":sQuery(id+"F23.wireOp",EDGE,"E54")}),-1.0]])]});
            var Q2;
            Q2=makeQuery(id+"F23.imprint","IMPRINT",FACE,{"disambiguationData":[TD([[makeQuery(id+"F23.imprint","IMPRINT",EDGE,{"derivedFrom":sQuery(id+"F23.wireOp",EDGE,"E53")}),-1.0]])]});
            var Q3;
            Q3=makeQuery(id+"F23.imprint","IMPRINT",FACE,{"disambiguationData":[TD([[makeQuery(id+"F23.imprint","IMPRINT",EDGE,{"derivedFrom":sQuery(id+"F23.wireOp",EDGE,"E52")}),-1.0]])]});
            var Q4;
            Q4=makeQuery(id+"F23.imprint","IMPRINT",FACE,{"disambiguationData":[TD([[makeQuery(id+"F23.imprint","IMPRINT",EDGE,{"derivedFrom":sQuery(id+"F23.wireOp",EDGE,"E50")}),-1.0]])]});
            var Q5;
            Q5=makeQuery(id+"F23.imprint","IMPRINT",FACE,{"disambiguationData":[TD([[makeQuery(id+"F23.imprint","IMPRINT",EDGE,{"derivedFrom":sQuery(id+"F23.wireOp",EDGE,"E51")}),-1.0]])]});
            var Q6;
            Q6=makeQuery(id+"F23.imprint","IMPRINT",FACE,{"disambiguationData":[TD([[makeQuery(id+"F23.imprint","IMPRINT",EDGE,{"derivedFrom":sQuery(id+"F23.wireOp",EDGE,"E49")}),-1.0]])]});
            var Q7;
            Q7=makeQuery(id+"F23.imprint","IMPRINT",FACE,{"disambiguationData":[TD([[makeQuery(id+"F23.imprint","IMPRINT",EDGE,{"derivedFrom":sQuery(id+"F23.wireOp",EDGE,"E48")}),-1.0]])]});
            var Q8;
            Q8=makeQuery(id+"F23.imprint","IMPRINT",FACE,{"disambiguationData":[TD([[makeQuery(id+"F23.imprint","IMPRINT",EDGE,{"derivedFrom":sQuery(id+"F23.wireOp",EDGE,"E58")}),-1.0]])]});
            var Q9;
            Q9=makeQuery(id+"F23.imprint","IMPRINT",FACE,{"disambiguationData":[TD([[makeQuery(id+"F23.imprint","IMPRINT",EDGE,{"derivedFrom":sQuery(id+"F23.wireOp",EDGE,"E57")}),-1.0]])]});
            var Q10;
            Q10=makeQuery(id+"F23.imprint","IMPRINT",FACE,{"disambiguationData":[TD([[makeQuery(id+"F23.imprint","IMPRINT",EDGE,{"derivedFrom":sQuery(id+"F23.wireOp",EDGE,"E59")}),-1.0]])]});
            var Q11;
            Q11=makeQuery(id+"F23.imprint","IMPRINT",FACE,{"disambiguationData":[TD([[makeQuery(id+"F23.imprint","IMPRINT",EDGE,{"derivedFrom":sQuery(id+"F23.wireOp",EDGE,"E56")}),-1.0]])]});
            var Q12;
            Q12=makeQuery(id+"F23.imprint","IMPRINT",FACE,{"disambiguationData":[TD([[makeQuery(id+"F23.imprint","IMPRINT",EDGE,{"derivedFrom":sQuery(id+"F23.wireOp",EDGE,"E62")}),-1.0]])]});
            var Q13;
            Q13=makeQuery(id+"F23.imprint","IMPRINT",FACE,{"disambiguationData":[TD([[makeQuery(id+"F23.imprint","IMPRINT",EDGE,{"derivedFrom":sQuery(id+"F23.wireOp",EDGE,"E61")}),-1.0]])]});
            var Q14;
            Q14=makeQuery(id+"F23.imprint","IMPRINT",FACE,{"disambiguationData":[TD([[makeQuery(id+"F23.imprint","IMPRINT",EDGE,{"derivedFrom":sQuery(id+"F23.wireOp",EDGE,"E63")}),-1.0]])]});
            var Q15;
            Q15=makeQuery(id+"F23.imprint","IMPRINT",FACE,{"disambiguationData":[TD([[makeQuery(id+"F23.imprint","IMPRINT",EDGE,{"derivedFrom":sQuery(id+"F23.wireOp",EDGE,"E60")}),-1.0]])]});
            var Q16;
            Q16=sQuery(id+"F23.wireOp",EDGE,"E70");
            var Q17;
            Q17=sQuery(id+"F23.wireOp",EDGE,"E71");
            var Q18;
            Q18=sQuery(id+"F23.wireOp",EDGE,"E68");
            var Q19;
            Q19=sQuery(id+"F23.wireOp",EDGE,"E69");
            var Q20;
            Q20=sQuery(id+"F23.wireOp",EDGE,"E66");
            var Q21;
            Q21=sQuery(id+"F23.wireOp",EDGE,"E67");
            var Q22;
            Q22=sQuery(id+"F23.wireOp",EDGE,"E64");
            var Q23;
            Q23=sQuery(id+"F23.wireOp",EDGE,"E65");
            extrude(context, id + "F31", {"entities" : qUnion([Q0, Q1, Q2, Q3, Q4, Q5, Q6, Q7, Q8, Q9, Q10, Q11, Q12, Q13, Q14, Q15]), "operationType" : NewBodyOperationType.ADD, "surfaceEntities" : qUnion([Q16, Q17, Q18, Q19, Q20, Q21, Q22, Q23]), "depth" : 6 * mm});
        }
        {
            var Q0;
            Q0=makeQuery(id+"F28.opExtrude","SWEPT_FACE",FACE,{"disambiguationData":[OSD([sQuery(id+"F23.wireOp",EDGE,"E45.top")])]});
            var sketch = newSketch(context, id + "F32", { "sketchPlane" : qUnion([Q0])});
            skCircle(sketch, "E174", {"center": v(-125.67, 27.5) * mm, "radius": 2.02 * mm});
            skCircle(sketch, "E175", {"center": v(-87.67, 27.5) * mm, "radius": 2.02 * mm});
            skCircle(sketch, "E176", {"center": v(-125.67, 5.5) * mm, "radius": 2.02 * mm});
            skCircle(sketch, "E177", {"center": v(-87.67, 5.5) * mm, "radius": 2.02 * mm});
            skSolve(sketch);
        }
        {
            var Q0;
            Q0=makeQuery(id+"F32.imprint","IMPRINT",FACE,{"disambiguationData":[TD([[makeQuery(id+"F32.imprint","IMPRINT",EDGE,{"derivedFrom":sQuery(id+"F32.wireOp",EDGE,"E174")}),1.0]])]});
            var Q1;
            Q1=makeQuery(id+"F32.imprint","IMPRINT",FACE,{"disambiguationData":[TD([[makeQuery(id+"F32.imprint","IMPRINT",EDGE,{"derivedFrom":sQuery(id+"F32.wireOp",EDGE,"E176")}),1.0]])]});
            var Q2;
            Q2=makeQuery(id+"F32.imprint","IMPRINT",FACE,{"disambiguationData":[TD([[makeQuery(id+"F32.imprint","IMPRINT",EDGE,{"derivedFrom":sQuery(id+"F32.wireOp",EDGE,"E177")}),1.0]])]});
            var Q3;
            Q3=makeQuery(id+"F32.imprint","IMPRINT",FACE,{"disambiguationData":[TD([[makeQuery(id+"F32.imprint","IMPRINT",EDGE,{"derivedFrom":sQuery(id+"F32.wireOp",EDGE,"E175")}),1.0]])]});
            extrude(context, id + "F33", {"entities" : qUnion([Q0, Q1, Q2, Q3]), "operationType" : NewBodyOperationType.REMOVE, "oppositeDirection" : true, "depth" : 17 * mm});
        }
        {
            var Q0;
            Q0=makeQuery(id+"F23.imprint","IMPRINT",FACE,{"disambiguationData":[TD([[makeQuery(id+"F23.imprint","IMPRINT",EDGE,{"derivedFrom":sQuery(id+"F23.wireOp",EDGE,"E80")}),-1.0]])]});
            var Q1;
            Q1=makeQuery(id+"F23.imprint","IMPRINT",FACE,{"disambiguationData":[TD([[makeQuery(id+"F23.imprint","IMPRINT",EDGE,{"derivedFrom":sQuery(id+"F23.wireOp",EDGE,"E82")}),-1.0]])]});
            var Q2;
            Q2=makeQuery(id+"F23.imprint","IMPRINT",FACE,{"disambiguationData":[TD([[makeQuery(id+"F23.imprint","IMPRINT",EDGE,{"derivedFrom":sQuery(id+"F23.wireOp",EDGE,"E81")}),-1.0]])]});
            var Q3;
            Q3=makeQuery(id+"F23.imprint","IMPRINT",FACE,{"disambiguationData":[TD([[makeQuery(id+"F23.imprint","IMPRINT",EDGE,{"derivedFrom":sQuery(id+"F23.wireOp",EDGE,"E83")}),-1.0]])]});
            extrude(context, id + "F34", {"entities" : qUnion([Q0, Q1, Q2, Q3]), "operationType" : NewBodyOperationType.ADD, "depth" : 8 * mm});
        }
        {
            var Q0;
            Q0=makeQuery(id+"F23.imprint","IMPRINT",FACE,{"disambiguationData":[TD([[makeQuery(id+"F23.imprint","IMPRINT",EDGE,{"derivedFrom":sQuery(id+"F23.wireOp",EDGE,"E88.bottom")}),-1.0]])]});
            extrude(context, id + "F35", {"entities" : qUnion([Q0]), "depth" : 63 * mm});
        }
        {
            var Q0;
            Q0=makeQuery(id+"F23.imprint","IMPRINT",FACE,{"disambiguationData":[TD([[makeQuery(id+"F23.imprint","IMPRINT",EDGE,{"derivedFrom":sQuery(id+"F23.wireOp",EDGE,"E90")}),1.0]])]});
            var Q1;
            Q1=makeQuery(id+"F23.imprint","IMPRINT",FACE,{"disambiguationData":[TD([[makeQuery(id+"F23.imprint","IMPRINT",EDGE,{"derivedFrom":sQuery(id+"F23.wireOp",EDGE,"E89")}),1.0]])]});
            var Q2;
            Q2=makeQuery(id+"F23.imprint","IMPRINT",FACE,{"disambiguationData":[TD([[makeQuery(id+"F23.imprint","IMPRINT",EDGE,{"derivedFrom":sQuery(id+"F23.wireOp",EDGE,"E92")}),1.0]])]});
            var Q3;
            Q3=makeQuery(id+"F23.imprint","IMPRINT",FACE,{"disambiguationData":[TD([[makeQuery(id+"F23.imprint","IMPRINT",EDGE,{"derivedFrom":sQuery(id+"F23.wireOp",EDGE,"E91")}),1.0]])]});
            extrude(context, id + "F36", {"entities" : qUnion([Q0, Q1, Q2, Q3]), "operationType" : NewBodyOperationType.ADD, "depth" : 58 * mm});
        }
        {
            var Q0;
            Q0=makeQuery(id+"F23.imprint","IMPRINT",FACE,{"disambiguationData":[TD([[makeQuery(id+"F23.imprint","IMPRINT",EDGE,{"derivedFrom":sQuery(id+"F23.wireOp",EDGE,"E88.bottom")}),-1.0]])]});
            var sketch = newSketch(context, id + "F37", { "sketchPlane" : qUnion([Q0])});
            skLineSegment(sketch, "E178.bottom", {"start": v(-8.76, -937.61) * mm, "end": v(-66.26, -937.61) * mm});
            skLineSegment(sketch, "E178.top", {"start": v(-8.76, -995.11) * mm, "end": v(-66.26, -995.11) * mm});
            skLineSegment(sketch, "E178.left", {"start": v(-8.76, -937.61) * mm, "end": v(-8.76, -995.11) * mm});
            skLineSegment(sketch, "E178.right", {"start": v(-66.26, -937.61) * mm, "end": v(-66.26, -995.11) * mm});
            skSolve(sketch);
        }
        {
            var Q0;
            Q0=makeQuery(id+"F37.imprint","IMPRINT",FACE,{"disambiguationData":[TD([[makeQuery(id+"F37.imprint","IMPRINT",EDGE,{"derivedFrom":sQuery(id+"F37.wireOp",EDGE,"E178.bottom")}),1.0]])]});
            extrude(context, id + "F38", {"entities" : qUnion([Q0]), "operationType" : NewBodyOperationType.ADD, "oppositeDirection" : true, "depth" : 29 * mm});
        }
        {
            var Q0;
            Q0=makeQuery(id+"F23.imprint","IMPRINT",FACE,{"disambiguationData":[TD([[makeQuery(id+"F23.imprint","IMPRINT",EDGE,{"derivedFrom":sQuery(id+"F23.wireOp",EDGE,"E91")}),1.0]])]});
            var Q1;
            Q1=makeQuery(id+"F23.imprint","IMPRINT",FACE,{"disambiguationData":[TD([[makeQuery(id+"F23.imprint","IMPRINT",EDGE,{"derivedFrom":sQuery(id+"F23.wireOp",EDGE,"E92")}),1.0]])]});
            extrude(context, id + "F39", {"entities" : qUnion([Q0, Q1]), "operationType" : NewBodyOperationType.ADD, "oppositeDirection" : true, "depth" : 29 * mm});
        }
        {
            var Q0;
            Q0=makeQuery(id+"F35.opExtrude","SWEPT_FACE",FACE,{"disambiguationData":[OSD([sQuery(id+"F23.wireOp",EDGE,"E88.top")])]});
            var sketch = newSketch(context, id + "F40", { "sketchPlane" : qUnion([Q0])});
            skCircle(sketch, "E179", {"center": v(-37.51, 31.5) * mm, "radius": 28 * mm});
            skPoint(sketch, "E180", {"position": v(-77.51, 31.5) * mm});
            skPoint(sketch, "E181", {"position": v(-37.51, 63) * mm});
            skLineSegment(sketch, "E182", {"start": v(-77.51, 31.5) * mm, "end": v(2.49, 31.5) * mm});
            skLineSegment(sketch, "E183", {"start": v(-37.51, 63) * mm, "end": v(-37.51, 0) * mm});
            skCircle(sketch, "E184", {"center": v(-37.51, 31.5) * mm, "radius": 17.5 * mm});
            skSolve(sketch);
        }
        {
            var Q0;
            {var subQ0=sQuery(id+"F40.wireOp",EDGE,"E184");var subQ3=sQuery(id+"F40.wireOp",EDGE,"E182");var subQ4=makeQuery(id+"F40.imprint","INTERSECT",VERTEX,{"disambiguationData":[OD(0.0)],"derivedFrom":[subQ3,subQ0]});Q0=makeQuery(id+"F40.imprint","IMPRINT",FACE,{"disambiguationData":[TD([[makeQuery(id+"F40.imprint","IMPRINT",EDGE,{"disambiguationData":[TD([[subQ4,-1.0]])],"derivedFrom":subQ3}),1.0]])]});}
            var Q1;
            {var subQ1=sQuery(id+"F40.wireOp",EDGE,"E183");var subQ3=sQuery(id+"F40.wireOp",EDGE,"E182");var subQ5=makeQuery(id+"F40.imprint","INTERSECT",VERTEX,{"derivedFrom":[subQ3,subQ1]});Q1=makeQuery(id+"F40.imprint","IMPRINT",FACE,{"disambiguationData":[TD([[makeQuery(id+"F40.imprint","IMPRINT",EDGE,{"disambiguationData":[TD([[subQ5,-1.0]])],"derivedFrom":subQ3}),1.0]])]});}
            var Q2;
            {var subQ0=sQuery(id+"F40.wireOp",EDGE,"E184");var subQ3=sQuery(id+"F40.wireOp",EDGE,"E182");var subQ4=makeQuery(id+"F40.imprint","INTERSECT",VERTEX,{"disambiguationData":[OD(0.0)],"derivedFrom":[subQ3,subQ0]});Q2=makeQuery(id+"F40.imprint","IMPRINT",FACE,{"disambiguationData":[TD([[makeQuery(id+"F40.imprint","IMPRINT",EDGE,{"disambiguationData":[TD([[subQ4,-1.0]])],"derivedFrom":subQ3}),-1.0]])]});}
            var Q3;
            {var subQ0=sQuery(id+"F40.wireOp",EDGE,"E183");var subQ3=sQuery(id+"F40.wireOp",EDGE,"E182");var subQ4=makeQuery(id+"F40.imprint","INTERSECT",VERTEX,{"derivedFrom":[subQ3,subQ0]});Q3=makeQuery(id+"F40.imprint","IMPRINT",FACE,{"disambiguationData":[TD([[makeQuery(id+"F40.imprint","IMPRINT",EDGE,{"disambiguationData":[TD([[subQ4,-1.0]])],"derivedFrom":subQ3}),-1.0]])]});}
            extrude(context, id + "F41", {"entities" : qUnion([Q0, Q1, Q2, Q3]), "operationType" : NewBodyOperationType.ADD, "depth" : 62.5 * mm});
        }
        {
            var Q0;
            {var subQ3=sQuery(id+"F40.wireOp",EDGE,"E182");var subQ5=sQuery(id+"F40.wireOp",EDGE,"E179");var subQ7=makeQuery(id+"F40.imprint","INTERSECT",VERTEX,{"disambiguationData":[OD(1.0)],"derivedFrom":[subQ5,subQ3]});Q0=makeQuery(id+"F40.imprint","IMPRINT",FACE,{"disambiguationData":[TD([[makeQuery(id+"F40.imprint","IMPRINT",EDGE,{"disambiguationData":[TD([[subQ7,-1.0]])],"derivedFrom":subQ5}),1.0]])]});}
            var Q1;
            {var subQ0=sQuery(id+"F40.wireOp",EDGE,"E183");var subQ3=sQuery(id+"F40.wireOp",EDGE,"E179");var subQ4=makeQuery(id+"F40.imprint","INTERSECT",VERTEX,{"disambiguationData":[OD(0.0)],"derivedFrom":[subQ3,subQ0]});Q1=makeQuery(id+"F40.imprint","IMPRINT",FACE,{"disambiguationData":[TD([[makeQuery(id+"F40.imprint","IMPRINT",EDGE,{"disambiguationData":[TD([[subQ4,-1.0]])],"derivedFrom":subQ3}),1.0]])]});}
            var Q2;
            {var subQ1=sQuery(id+"F40.wireOp",EDGE,"E183");var subQ5=sQuery(id+"F40.wireOp",EDGE,"E179");var subQ6=makeQuery(id+"F40.imprint","INTERSECT",VERTEX,{"disambiguationData":[OD(0.0)],"derivedFrom":[subQ5,subQ1]});Q2=makeQuery(id+"F40.imprint","IMPRINT",FACE,{"disambiguationData":[TD([[makeQuery(id+"F40.imprint","IMPRINT",EDGE,{"disambiguationData":[TD([[subQ6,1.0]])],"derivedFrom":subQ5}),1.0]])]});}
            var Q3;
            {var subQ3=sQuery(id+"F40.wireOp",EDGE,"E182");var subQ5=sQuery(id+"F40.wireOp",EDGE,"E179");var subQ7=makeQuery(id+"F40.imprint","INTERSECT",VERTEX,{"disambiguationData":[OD(0.0)],"derivedFrom":[subQ5,subQ3]});Q3=makeQuery(id+"F40.imprint","IMPRINT",FACE,{"disambiguationData":[TD([[makeQuery(id+"F40.imprint","IMPRINT",EDGE,{"disambiguationData":[TD([[subQ7,1.0]])],"derivedFrom":subQ5}),1.0]])]});}
            extrude(context, id + "F42", {"entities" : qUnion([Q0, Q1, Q2, Q3]), "operationType" : NewBodyOperationType.ADD, "depth" : 30.5 * mm});
        }
        {
            var Q0;
            Q0=makeQuery(id+"F23.imprint","IMPRINT",FACE,{"disambiguationData":[TD([[makeQuery(id+"F23.imprint","IMPRINT",EDGE,{"derivedFrom":sQuery(id+"F23.wireOp",EDGE,"E93.bottom")}),-1.0]])]});
            extrude(context, id + "F43", {"entities" : qUnion([Q0]), "depth" : 6.5 * mm});
        }
        {
            var Q0;
            Q0=makeQuery(id+"F23.imprint","IMPRINT",FACE,{"disambiguationData":[TD([[makeQuery(id+"F23.imprint","IMPRINT",EDGE,{"derivedFrom":sQuery(id+"F23.wireOp",EDGE,"E93.bottom")}),-1.0]])]});
            var sketch = newSketch(context, id + "F44", { "sketchPlane" : qUnion([Q0])});
            skLineSegment(sketch, "E185.bottom", {"start": v(120.31, -999.03) * mm, "end": v(111.81, -999.03) * mm});
            skLineSegment(sketch, "E185.top", {"start": v(120.31, -1042.03) * mm, "end": v(111.81, -1042.03) * mm});
            skLineSegment(sketch, "E185.left", {"start": v(120.31, -999.03) * mm, "end": v(120.31, -1042.03) * mm});
            skLineSegment(sketch, "E185.right", {"start": v(111.81, -999.03) * mm, "end": v(111.81, -1042.03) * mm});
            skLineSegment(sketch, "E186.bottom", {"start": v(96.81, -999.03) * mm, "end": v(88.31, -999.03) * mm});
            skLineSegment(sketch, "E186.top", {"start": v(96.81, -1042.03) * mm, "end": v(88.31, -1042.03) * mm});
            skLineSegment(sketch, "E186.left", {"start": v(96.81, -999.03) * mm, "end": v(96.81, -1042.03) * mm});
            skLineSegment(sketch, "E186.right", {"start": v(88.31, -999.03) * mm, "end": v(88.31, -1042.03) * mm});
            skSolve(sketch);
        }
        {
            var Q0;
            Q0 = qSketchRegion(id + "F44", true);
            extrude(context, id + "F45", {"entities" : qUnion([Q0]), "operationType" : NewBodyOperationType.ADD, "oppositeDirection" : true, "depth" : 5.5 * mm});
        }
        {
            var Q0;
            Q0=makeQuery(id+"F43.opExtrude","CAP_FACE",FACE,{"disambiguationData":[OSD([sQuery(id+"F23.wireOp",EDGE,"E93.bottom"),sQuery(id+"F23.wireOp",EDGE,"E93.top"),sQuery(id+"F23.wireOp",EDGE,"E93.left"),sQuery(id+"F23.wireOp",EDGE,"E93.right")])],"isStart":false});
            var sketch = newSketch(context, id + "F46", { "sketchPlane" : qUnion([Q0])});
            skCircle(sketch, "E187", {"center": v(91.81, -1010.53) * mm, "radius": 1.34 * mm});
            skCircle(sketch, "E188", {"center": v(116.81, -1010.53) * mm, "radius": 1.34 * mm});
            skCircle(sketch, "E189", {"center": v(91.81, -1030.53) * mm, "radius": 1.34 * mm});
            skCircle(sketch, "E190", {"center": v(116.81, -1030.53) * mm, "radius": 1.34 * mm});
            skSolve(sketch);
        }
        {
            var Q0;
            Q0=makeQuery(id+"F46.imprint","IMPRINT",FACE,{"disambiguationData":[TD([[makeQuery(id+"F46.imprint","IMPRINT",EDGE,{"derivedFrom":sQuery(id+"F46.wireOp",EDGE,"E189")}),1.0]])]});
            var Q1;
            Q1=makeQuery(id+"F46.imprint","IMPRINT",FACE,{"disambiguationData":[TD([[makeQuery(id+"F46.imprint","IMPRINT",EDGE,{"derivedFrom":sQuery(id+"F46.wireOp",EDGE,"E187")}),1.0]])]});
            var Q2;
            Q2=makeQuery(id+"F46.imprint","IMPRINT",FACE,{"disambiguationData":[TD([[makeQuery(id+"F46.imprint","IMPRINT",EDGE,{"derivedFrom":sQuery(id+"F46.wireOp",EDGE,"E188")}),1.0]])]});
            var Q3;
            Q3=makeQuery(id+"F46.imprint","IMPRINT",FACE,{"disambiguationData":[TD([[makeQuery(id+"F46.imprint","IMPRINT",EDGE,{"derivedFrom":sQuery(id+"F46.wireOp",EDGE,"E190")}),1.0]])]});
            var Q4;
            Q4=sQuery(id+"F46.wireOp",EDGE,"E187");
            var Q5;
            Q5=sQuery(id+"F46.wireOp",EDGE,"E189");
            var Q6;
            Q6=sQuery(id+"F46.wireOp",EDGE,"E190");
            var Q7;
            Q7=sQuery(id+"F46.wireOp",EDGE,"E188");
            extrude(context, id + "F47", {"entities" : qUnion([Q0, Q1, Q2, Q3]), "operationType" : NewBodyOperationType.REMOVE, "surfaceEntities" : qUnion([Q4, Q5, Q6, Q7]), "oppositeDirection" : true, "depth" : 4 * mm});
        }
        {
            var Q0;
            Q0=makeQuery(id+"F23.imprint","IMPRINT",FACE,{"disambiguationData":[TD([[makeQuery(id+"F23.imprint","IMPRINT",EDGE,{"derivedFrom":sQuery(id+"F23.wireOp",EDGE,"E94.bottom")}),-1.0]])]});
            extrude(context, id + "F48", {"entities" : qUnion([Q0]), "depth" : 9.5 * mm});
        }
        {
            var Q0;
            Q0=makeQuery(id+"F48.opExtrude","CAP_FACE",FACE,{"disambiguationData":[OSD([sQuery(id+"F23.wireOp",EDGE,"E94.bottom"),sQuery(id+"F23.wireOp",EDGE,"E94.top"),sQuery(id+"F23.wireOp",EDGE,"E94.left"),sQuery(id+"F23.wireOp",EDGE,"E94.right"),sQuery(id+"F23.wireOp",EDGE,"E95"),sQuery(id+"F23.wireOp",EDGE,"E96"),sQuery(id+"F23.wireOp",EDGE,"E97"),sQuery(id+"F23.wireOp",EDGE,"E98"),sQuery(id+"F23.wireOp",EDGE,"E99"),sQuery(id+"F23.wireOp",EDGE,"E100"),sQuery(id+"F23.wireOp",EDGE,"E101"),sQuery(id+"F23.wireOp",EDGE,"E102"),sQuery(id+"F23.wireOp",EDGE,"E103"),sQuery(id+"F23.wireOp",EDGE,"E104"),sQuery(id+"F23.wireOp",EDGE,"E105"),sQuery(id+"F23.wireOp",EDGE,"E106"),sQuery(id+"F23.wireOp",EDGE,"E107")])],"isStart":false});
            var sketch = newSketch(context, id + "F49", { "sketchPlane" : qUnion([Q0])});
            skCircle(sketch, "E191", {"center": v(174.82, -746.35) * mm, "radius": 3 * mm});
            skCircle(sketch, "E192", {"center": v(174.82, -786.35) * mm, "radius": 3 * mm});
            skCircle(sketch, "E193", {"center": v(174.82, -826.35) * mm, "radius": 3 * mm});
            skCircle(sketch, "E194", {"center": v(174.82, -866.35) * mm, "radius": 3 * mm});
            skCircle(sketch, "E195", {"center": v(174.82, -906.35) * mm, "radius": 3 * mm});
            skCircle(sketch, "E196", {"center": v(174.82, -946.35) * mm, "radius": 3 * mm});
            skCircle(sketch, "E197", {"center": v(174.82, -986.35) * mm, "radius": 3 * mm});
            skCircle(sketch, "E198", {"center": v(174.82, -1026.35) * mm, "radius": 3 * mm});
            skCircle(sketch, "E199", {"center": v(174.82, -1066.35) * mm, "radius": 3 * mm});
            skCircle(sketch, "E200", {"center": v(174.82, -1106.35) * mm, "radius": 3 * mm});
            skCircle(sketch, "E201", {"center": v(174.82, -1146.35) * mm, "radius": 3 * mm});
            skCircle(sketch, "E202", {"center": v(174.82, -1186.35) * mm, "radius": 3 * mm});
            skCircle(sketch, "E203", {"center": v(174.82, -1226.35) * mm, "radius": 3 * mm});
            skSolve(sketch);
        }
        {
            var Q0;
            Q0=makeQuery(id+"F49.imprint","IMPRINT",FACE,{"disambiguationData":[TD([[makeQuery(id+"F49.imprint","IMPRINT",EDGE,{"derivedFrom":sQuery(id+"F49.wireOp",EDGE,"E191")}),1.0]])]});
            var Q1;
            Q1=makeQuery(id+"F49.imprint","IMPRINT",FACE,{"disambiguationData":[TD([[makeQuery(id+"F49.imprint","IMPRINT",EDGE,{"derivedFrom":sQuery(id+"F49.wireOp",EDGE,"E192")}),1.0]])]});
            var Q2;
            Q2=makeQuery(id+"F49.imprint","IMPRINT",FACE,{"disambiguationData":[TD([[makeQuery(id+"F49.imprint","IMPRINT",EDGE,{"derivedFrom":sQuery(id+"F49.wireOp",EDGE,"E193")}),1.0]])]});
            var Q3;
            Q3=makeQuery(id+"F49.imprint","IMPRINT",FACE,{"disambiguationData":[TD([[makeQuery(id+"F49.imprint","IMPRINT",EDGE,{"derivedFrom":sQuery(id+"F49.wireOp",EDGE,"E194")}),1.0]])]});
            var Q4;
            Q4=makeQuery(id+"F49.imprint","IMPRINT",FACE,{"disambiguationData":[TD([[makeQuery(id+"F49.imprint","IMPRINT",EDGE,{"derivedFrom":sQuery(id+"F49.wireOp",EDGE,"E195")}),1.0]])]});
            var Q5;
            Q5=makeQuery(id+"F49.imprint","IMPRINT",FACE,{"disambiguationData":[TD([[makeQuery(id+"F49.imprint","IMPRINT",EDGE,{"derivedFrom":sQuery(id+"F49.wireOp",EDGE,"E196")}),1.0]])]});
            var Q6;
            Q6=makeQuery(id+"F49.imprint","IMPRINT",FACE,{"disambiguationData":[TD([[makeQuery(id+"F49.imprint","IMPRINT",EDGE,{"derivedFrom":sQuery(id+"F49.wireOp",EDGE,"E197")}),1.0]])]});
            var Q7;
            Q7=makeQuery(id+"F49.imprint","IMPRINT",FACE,{"disambiguationData":[TD([[makeQuery(id+"F49.imprint","IMPRINT",EDGE,{"derivedFrom":sQuery(id+"F49.wireOp",EDGE,"E198")}),1.0]])]});
            var Q8;
            Q8=makeQuery(id+"F49.imprint","IMPRINT",FACE,{"disambiguationData":[TD([[makeQuery(id+"F49.imprint","IMPRINT",EDGE,{"derivedFrom":sQuery(id+"F49.wireOp",EDGE,"E199")}),1.0]])]});
            var Q9;
            Q9=makeQuery(id+"F49.imprint","IMPRINT",FACE,{"disambiguationData":[TD([[makeQuery(id+"F49.imprint","IMPRINT",EDGE,{"derivedFrom":sQuery(id+"F49.wireOp",EDGE,"E200")}),1.0]])]});
            var Q10;
            Q10=makeQuery(id+"F49.imprint","IMPRINT",FACE,{"disambiguationData":[TD([[makeQuery(id+"F49.imprint","IMPRINT",EDGE,{"derivedFrom":sQuery(id+"F49.wireOp",EDGE,"E201")}),1.0]])]});
            var Q11;
            Q11=makeQuery(id+"F49.imprint","IMPRINT",FACE,{"disambiguationData":[TD([[makeQuery(id+"F49.imprint","IMPRINT",EDGE,{"derivedFrom":sQuery(id+"F49.wireOp",EDGE,"E202")}),1.0]])]});
            var Q12;
            Q12=makeQuery(id+"F49.imprint","IMPRINT",FACE,{"disambiguationData":[TD([[makeQuery(id+"F49.imprint","IMPRINT",EDGE,{"derivedFrom":sQuery(id+"F49.wireOp",EDGE,"E203")}),1.0]])]});
            var Q13;
            Q13=sQuery(id+"F49.wireOp",EDGE,"E191");
            var Q14;
            Q14=sQuery(id+"F49.wireOp",EDGE,"E192");
            var Q15;
            Q15=sQuery(id+"F49.wireOp",EDGE,"E193");
            var Q16;
            Q16=sQuery(id+"F49.wireOp",EDGE,"E194");
            var Q17;
            Q17=sQuery(id+"F49.wireOp",EDGE,"E195");
            var Q18;
            Q18=sQuery(id+"F49.wireOp",EDGE,"E196");
            var Q19;
            Q19=sQuery(id+"F49.wireOp",EDGE,"E197");
            var Q20;
            Q20=sQuery(id+"F49.wireOp",EDGE,"E198");
            var Q21;
            Q21=sQuery(id+"F49.wireOp",EDGE,"E199");
            var Q22;
            Q22=sQuery(id+"F49.wireOp",EDGE,"E200");
            var Q23;
            Q23=sQuery(id+"F49.wireOp",EDGE,"E201");
            var Q24;
            Q24=sQuery(id+"F49.wireOp",EDGE,"E202");
            var Q25;
            Q25=sQuery(id+"F49.wireOp",EDGE,"E203");
            extrude(context, id + "F50", {"entities" : qUnion([Q0, Q1, Q2, Q3, Q4, Q5, Q6, Q7, Q8, Q9, Q10, Q11, Q12]), "operationType" : NewBodyOperationType.REMOVE, "surfaceEntities" : qUnion([Q13, Q14, Q15, Q16, Q17, Q18, Q19, Q20, Q21, Q22, Q23, Q24, Q25]), "oppositeDirection" : true, "depth" : 4.7 * mm});
        }
        {
            var Q0;
            Q0=makeQuery(id+"F23.imprint","IMPRINT",FACE,{"disambiguationData":[TD([[makeQuery(id+"F23.imprint","IMPRINT",EDGE,{"derivedFrom":sQuery(id+"F23.wireOp",EDGE,"E124.bottom")}),1.0]])]});
            extrude(context, id + "F51", {"entities" : qUnion([Q0]), "depth" : 30 * mm});
        }
        {
            var Q0;
            Q0=makeQuery(id+"F23.imprint","IMPRINT",FACE,{"disambiguationData":[TD([[makeQuery(id+"F23.imprint","IMPRINT",EDGE,{"derivedFrom":sQuery(id+"F23.wireOp",EDGE,"E110.right")}),-1.0]])]});
            extrude(context, id + "F52", {"entities" : qUnion([Q0]), "operationType" : NewBodyOperationType.ADD, "depth" : 29 * mm});
        }
        {
            var Q0;
            Q0=makeQuery(id+"F52.opExtrude","CAP_FACE",FACE,{"disambiguationData":[OSD([sQuery(id+"F23.wireOp",EDGE,"E110.right"),sQuery(id+"F23.wireOp",EDGE,"E111"),sQuery(id+"F23.wireOp",EDGE,"E112"),sQuery(id+"F23.wireOp",EDGE,"E113"),sQuery(id+"F23.wireOp",EDGE,"E114"),sQuery(id+"F23.wireOp",EDGE,"E115"),sQuery(id+"F23.wireOp",EDGE,"E116"),sQuery(id+"F23.wireOp",EDGE,"E117"),sQuery(id+"F23.wireOp",EDGE,"E118"),sQuery(id+"F23.wireOp",EDGE,"E110.top"),sQuery(id+"F23.wireOp",EDGE,"E119"),sQuery(id+"F23.wireOp",EDGE,"E120"),sQuery(id+"F23.wireOp",EDGE,"E121"),sQuery(id+"F23.wireOp",EDGE,"E122"),sQuery(id+"F23.wireOp",EDGE,"E123"),sQuery(id+"F23.wireOp",EDGE,"E110.bottom"),sQuery(id+"F23.wireOp",EDGE,"E110.left"),sQuery(id+"F23.wireOp",EDGE,"E125"),sQuery(id+"F23.wireOp",EDGE,"E126"),sQuery(id+"F23.wireOp",EDGE,"E127"),sQuery(id+"F23.wireOp",EDGE,"E128"),sQuery(id+"F23.wireOp",EDGE,"E129"),sQuery(id+"F23.wireOp",EDGE,"E130"),sQuery(id+"F23.wireOp",EDGE,"E131"),sQuery(id+"F23.wireOp",EDGE,"E132"),sQuery(id+"F23.wireOp",EDGE,"E133"),sQuery(id+"F23.wireOp",EDGE,"E134"),sQuery(id+"F23.wireOp",EDGE,"E135"),sQuery(id+"F23.wireOp",EDGE,"E136")])],"isStart":false});
            var sketch = newSketch(context, id + "F53", { "sketchPlane" : qUnion([Q0])});
            skCircle(sketch, "E204", {"center": v(277.23, -768.77) * mm, "radius": 5 * mm});
            skCircle(sketch, "E205", {"center": v(277.23, -808.77) * mm, "radius": 5 * mm});
            skCircle(sketch, "E206", {"center": v(277.23, -848.77) * mm, "radius": 5 * mm});
            skCircle(sketch, "E207", {"center": v(277.23, -888.77) * mm, "radius": 5 * mm});
            skCircle(sketch, "E208", {"center": v(277.23, -928.77) * mm, "radius": 5 * mm});
            skCircle(sketch, "E209", {"center": v(277.23, -968.77) * mm, "radius": 5 * mm});
            skCircle(sketch, "E210", {"center": v(277.23, -1008.77) * mm, "radius": 5 * mm});
            skCircle(sketch, "E211", {"center": v(277.23, -1048.77) * mm, "radius": 5 * mm});
            skCircle(sketch, "E212", {"center": v(277.23, -1088.77) * mm, "radius": 5 * mm});
            skCircle(sketch, "E213", {"center": v(277.23, -1128.77) * mm, "radius": 5 * mm});
            skCircle(sketch, "E214", {"center": v(277.23, -1168.77) * mm, "radius": 5 * mm});
            skCircle(sketch, "E215", {"center": v(277.23, -1208.77) * mm, "radius": 5 * mm});
            skSolve(sketch);
        }
        {
            var Q0;
            Q0=makeQuery(id+"F53.imprint","IMPRINT",FACE,{"disambiguationData":[TD([[makeQuery(id+"F53.imprint","IMPRINT",EDGE,{"derivedFrom":sQuery(id+"F53.wireOp",EDGE,"E204")}),1.0]])]});
            var Q1;
            Q1=makeQuery(id+"F53.imprint","IMPRINT",FACE,{"disambiguationData":[TD([[makeQuery(id+"F53.imprint","IMPRINT",EDGE,{"derivedFrom":sQuery(id+"F53.wireOp",EDGE,"E205")}),1.0]])]});
            var Q2;
            Q2=makeQuery(id+"F53.imprint","IMPRINT",FACE,{"disambiguationData":[TD([[makeQuery(id+"F53.imprint","IMPRINT",EDGE,{"derivedFrom":sQuery(id+"F53.wireOp",EDGE,"E206")}),1.0]])]});
            var Q3;
            Q3=makeQuery(id+"F53.imprint","IMPRINT",FACE,{"disambiguationData":[TD([[makeQuery(id+"F53.imprint","IMPRINT",EDGE,{"derivedFrom":sQuery(id+"F53.wireOp",EDGE,"E207")}),1.0]])]});
            var Q4;
            Q4=makeQuery(id+"F53.imprint","IMPRINT",FACE,{"disambiguationData":[TD([[makeQuery(id+"F53.imprint","IMPRINT",EDGE,{"derivedFrom":sQuery(id+"F53.wireOp",EDGE,"E208")}),1.0]])]});
            var Q5;
            Q5=makeQuery(id+"F53.imprint","IMPRINT",FACE,{"disambiguationData":[TD([[makeQuery(id+"F53.imprint","IMPRINT",EDGE,{"derivedFrom":sQuery(id+"F53.wireOp",EDGE,"E209")}),1.0]])]});
            var Q6;
            Q6=makeQuery(id+"F53.imprint","IMPRINT",FACE,{"disambiguationData":[TD([[makeQuery(id+"F53.imprint","IMPRINT",EDGE,{"derivedFrom":sQuery(id+"F53.wireOp",EDGE,"E210")}),1.0]])]});
            var Q7;
            Q7=makeQuery(id+"F53.imprint","IMPRINT",FACE,{"disambiguationData":[TD([[makeQuery(id+"F53.imprint","IMPRINT",EDGE,{"derivedFrom":sQuery(id+"F53.wireOp",EDGE,"E211")}),1.0]])]});
            var Q8;
            Q8=makeQuery(id+"F53.imprint","IMPRINT",FACE,{"disambiguationData":[TD([[makeQuery(id+"F53.imprint","IMPRINT",EDGE,{"derivedFrom":sQuery(id+"F53.wireOp",EDGE,"E212")}),1.0]])]});
            var Q9;
            Q9=makeQuery(id+"F53.imprint","IMPRINT",FACE,{"disambiguationData":[TD([[makeQuery(id+"F53.imprint","IMPRINT",EDGE,{"derivedFrom":sQuery(id+"F53.wireOp",EDGE,"E213")}),1.0]])]});
            var Q10;
            Q10=makeQuery(id+"F53.imprint","IMPRINT",FACE,{"disambiguationData":[TD([[makeQuery(id+"F53.imprint","IMPRINT",EDGE,{"derivedFrom":sQuery(id+"F53.wireOp",EDGE,"E214")}),1.0]])]});
            var Q11;
            Q11=makeQuery(id+"F53.imprint","IMPRINT",FACE,{"disambiguationData":[TD([[makeQuery(id+"F53.imprint","IMPRINT",EDGE,{"derivedFrom":sQuery(id+"F53.wireOp",EDGE,"E215")}),1.0]])]});
            extrude(context, id + "F54", {"entities" : qUnion([Q0, Q1, Q2, Q3, Q4, Q5, Q6, Q7, Q8, Q9, Q10, Q11]), "operationType" : NewBodyOperationType.REMOVE, "oppositeDirection" : true, "depth" : 6 * mm});
        }
        {
            var Q0;
            Q0=makeQuery(id+"F23.imprint","IMPRINT",FACE,{"disambiguationData":[TD([[makeQuery(id+"F23.imprint","IMPRINT",EDGE,{"derivedFrom":sQuery(id+"F23.wireOp",EDGE,"E137.bottom")}),-1.0]])]});
            extrude(context, id + "F55", {"entities" : qUnion([Q0]), "depth" : 15 * mm});
        }
        {
            var Q0;
            Q0=makeQuery(id+"F23.imprint","IMPRINT",FACE,{"disambiguationData":[TD([[makeQuery(id+"F23.imprint","IMPRINT",EDGE,{"derivedFrom":sQuery(id+"F23.wireOp",EDGE,"E164")}),-1.0]])]});
            var Q1;
            Q1=makeQuery(id+"F23.imprint","IMPRINT",FACE,{"disambiguationData":[TD([[makeQuery(id+"F23.imprint","IMPRINT",EDGE,{"derivedFrom":sQuery(id+"F23.wireOp",EDGE,"E163")}),-1.0]])]});
            var Q2;
            Q2=makeQuery(id+"F23.imprint","IMPRINT",FACE,{"disambiguationData":[TD([[makeQuery(id+"F23.imprint","IMPRINT",EDGE,{"derivedFrom":sQuery(id+"F23.wireOp",EDGE,"E166")}),-1.0]])]});
            var Q3;
            Q3=makeQuery(id+"F23.imprint","IMPRINT",FACE,{"disambiguationData":[TD([[makeQuery(id+"F23.imprint","IMPRINT",EDGE,{"derivedFrom":sQuery(id+"F23.wireOp",EDGE,"E165")}),-1.0]])]});
            var Q4;
            Q4=makeQuery(id+"F23.imprint","IMPRINT",FACE,{"disambiguationData":[TD([[makeQuery(id+"F23.imprint","IMPRINT",EDGE,{"derivedFrom":sQuery(id+"F23.wireOp",EDGE,"E171.1.0.3")}),-1.0]])]});
            var Q5;
            Q5=makeQuery(id+"F23.imprint","IMPRINT",FACE,{"disambiguationData":[TD([[makeQuery(id+"F23.imprint","IMPRINT",EDGE,{"derivedFrom":sQuery(id+"F23.wireOp",EDGE,"E171.1.0.1")}),-1.0]])]});
            var Q6;
            Q6=makeQuery(id+"F23.imprint","IMPRINT",FACE,{"disambiguationData":[TD([[makeQuery(id+"F23.imprint","IMPRINT",EDGE,{"derivedFrom":sQuery(id+"F23.wireOp",EDGE,"E171.1.0.4")}),1.0]])]});
            var Q7;
            Q7=makeQuery(id+"F23.imprint","IMPRINT",FACE,{"disambiguationData":[TD([[makeQuery(id+"F23.imprint","IMPRINT",EDGE,{"derivedFrom":sQuery(id+"F23.wireOp",EDGE,"E171.1.0.0")}),-1.0]])]});
            var Q8;
            Q8=makeQuery(id+"F23.imprint","IMPRINT",FACE,{"disambiguationData":[TD([[makeQuery(id+"F23.imprint","IMPRINT",EDGE,{"derivedFrom":sQuery(id+"F23.wireOp",EDGE,"E172.1.0.3")}),1.0]])]});
            var Q9;
            Q9=makeQuery(id+"F23.imprint","IMPRINT",FACE,{"disambiguationData":[TD([[makeQuery(id+"F23.imprint","IMPRINT",EDGE,{"derivedFrom":sQuery(id+"F23.wireOp",EDGE,"E172.1.0.12")}),1.0]])]});
            var Q10;
            Q10=makeQuery(id+"F23.imprint","IMPRINT",FACE,{"disambiguationData":[TD([[makeQuery(id+"F23.imprint","IMPRINT",EDGE,{"derivedFrom":sQuery(id+"F23.wireOp",EDGE,"E172.1.0.11")}),1.0]])]});
            var Q11;
            Q11=makeQuery(id+"F23.imprint","IMPRINT",FACE,{"disambiguationData":[TD([[makeQuery(id+"F23.imprint","IMPRINT",EDGE,{"derivedFrom":sQuery(id+"F23.wireOp",EDGE,"E172.1.0.4")}),1.0]])]});
            var Q12;
            Q12=makeQuery(id+"F23.imprint","IMPRINT",FACE,{"disambiguationData":[TD([[makeQuery(id+"F23.imprint","IMPRINT",EDGE,{"derivedFrom":sQuery(id+"F23.wireOp",EDGE,"E172.1.0.2")}),-1.0]])]});
            var Q13;
            Q13=makeQuery(id+"F23.imprint","IMPRINT",FACE,{"disambiguationData":[TD([[makeQuery(id+"F23.imprint","IMPRINT",EDGE,{"derivedFrom":sQuery(id+"F23.wireOp",EDGE,"E172.1.0.1")}),-1.0]])]});
            var Q14;
            Q14=makeQuery(id+"F23.imprint","IMPRINT",FACE,{"disambiguationData":[TD([[makeQuery(id+"F23.imprint","IMPRINT",EDGE,{"derivedFrom":sQuery(id+"F23.wireOp",EDGE,"E172.1.0.14")}),-1.0]])]});
            var Q15;
            Q15=makeQuery(id+"F23.imprint","IMPRINT",FACE,{"disambiguationData":[TD([[makeQuery(id+"F23.imprint","IMPRINT",EDGE,{"derivedFrom":sQuery(id+"F23.wireOp",EDGE,"E172.1.0.6")}),1.0]])]});
            var Q16;
            Q16=sQuery(id+"F23.wireOp",EDGE,"E167");
            extrude(context, id + "F56", {"entities" : qUnion([Q0, Q1, Q2, Q3, Q4, Q5, Q6, Q7, Q8, Q9, Q10, Q11, Q12, Q13, Q14, Q15]), "operationType" : NewBodyOperationType.ADD, "surfaceEntities" : qUnion([Q16]), "depth" : 15 * mm});
        }
        {
            var Q0;
            Q0=makeQuery(id+"F23.imprint","IMPRINT",FACE,{"disambiguationData":[TD([[makeQuery(id+"F23.imprint","IMPRINT",EDGE,{"derivedFrom":sQuery(id+"F23.wireOp",EDGE,"E164")}),-1.0]])]});
            var Q1;
            Q1=makeQuery(id+"F23.imprint","IMPRINT",FACE,{"disambiguationData":[TD([[makeQuery(id+"F23.imprint","IMPRINT",EDGE,{"derivedFrom":sQuery(id+"F23.wireOp",EDGE,"E163")}),-1.0]])]});
            var Q2;
            Q2=makeQuery(id+"F23.imprint","IMPRINT",FACE,{"disambiguationData":[TD([[makeQuery(id+"F23.imprint","IMPRINT",EDGE,{"derivedFrom":sQuery(id+"F23.wireOp",EDGE,"E166")}),-1.0]])]});
            var Q3;
            Q3=makeQuery(id+"F23.imprint","IMPRINT",FACE,{"disambiguationData":[TD([[makeQuery(id+"F23.imprint","IMPRINT",EDGE,{"derivedFrom":sQuery(id+"F23.wireOp",EDGE,"E165")}),-1.0]])]});
            var Q4;
            Q4=makeQuery(id+"F23.imprint","IMPRINT",FACE,{"disambiguationData":[TD([[makeQuery(id+"F23.imprint","IMPRINT",EDGE,{"derivedFrom":sQuery(id+"F23.wireOp",EDGE,"E171.1.0.3")}),-1.0]])]});
            var Q5;
            Q5=makeQuery(id+"F23.imprint","IMPRINT",FACE,{"disambiguationData":[TD([[makeQuery(id+"F23.imprint","IMPRINT",EDGE,{"derivedFrom":sQuery(id+"F23.wireOp",EDGE,"E171.1.0.1")}),-1.0]])]});
            var Q6;
            Q6=makeQuery(id+"F23.imprint","IMPRINT",FACE,{"disambiguationData":[TD([[makeQuery(id+"F23.imprint","IMPRINT",EDGE,{"derivedFrom":sQuery(id+"F23.wireOp",EDGE,"E171.1.0.4")}),1.0]])]});
            var Q7;
            Q7=makeQuery(id+"F23.imprint","IMPRINT",FACE,{"disambiguationData":[TD([[makeQuery(id+"F23.imprint","IMPRINT",EDGE,{"derivedFrom":sQuery(id+"F23.wireOp",EDGE,"E171.1.0.0")}),-1.0]])]});
            var Q8;
            Q8=makeQuery(id+"F23.imprint","IMPRINT",FACE,{"disambiguationData":[TD([[makeQuery(id+"F23.imprint","IMPRINT",EDGE,{"derivedFrom":sQuery(id+"F23.wireOp",EDGE,"E172.1.0.3")}),1.0]])]});
            var Q9;
            Q9=makeQuery(id+"F23.imprint","IMPRINT",FACE,{"disambiguationData":[TD([[makeQuery(id+"F23.imprint","IMPRINT",EDGE,{"derivedFrom":sQuery(id+"F23.wireOp",EDGE,"E172.1.0.12")}),1.0]])]});
            var Q10;
            Q10=makeQuery(id+"F23.imprint","IMPRINT",FACE,{"disambiguationData":[TD([[makeQuery(id+"F23.imprint","IMPRINT",EDGE,{"derivedFrom":sQuery(id+"F23.wireOp",EDGE,"E172.1.0.11")}),1.0]])]});
            var Q11;
            Q11=makeQuery(id+"F23.imprint","IMPRINT",FACE,{"disambiguationData":[TD([[makeQuery(id+"F23.imprint","IMPRINT",EDGE,{"derivedFrom":sQuery(id+"F23.wireOp",EDGE,"E172.1.0.4")}),1.0]])]});
            var Q12;
            Q12=makeQuery(id+"F23.imprint","IMPRINT",FACE,{"disambiguationData":[TD([[makeQuery(id+"F23.imprint","IMPRINT",EDGE,{"derivedFrom":sQuery(id+"F23.wireOp",EDGE,"E172.1.0.2")}),-1.0]])]});
            var Q13;
            Q13=makeQuery(id+"F23.imprint","IMPRINT",FACE,{"disambiguationData":[TD([[makeQuery(id+"F23.imprint","IMPRINT",EDGE,{"derivedFrom":sQuery(id+"F23.wireOp",EDGE,"E172.1.0.1")}),-1.0]])]});
            var Q14;
            Q14=makeQuery(id+"F23.imprint","IMPRINT",FACE,{"disambiguationData":[TD([[makeQuery(id+"F23.imprint","IMPRINT",EDGE,{"derivedFrom":sQuery(id+"F23.wireOp",EDGE,"E172.1.0.14")}),-1.0]])]});
            var Q15;
            Q15=makeQuery(id+"F23.imprint","IMPRINT",FACE,{"disambiguationData":[TD([[makeQuery(id+"F23.imprint","IMPRINT",EDGE,{"derivedFrom":sQuery(id+"F23.wireOp",EDGE,"E172.1.0.6")}),1.0]])]});
            extrude(context, id + "F57", {"entities" : qUnion([Q0, Q1, Q2, Q3, Q4, Q5, Q6, Q7, Q8, Q9, Q10, Q11, Q12, Q13, Q14, Q15]), "operationType" : NewBodyOperationType.REMOVE, "depth" : 6 * mm});
        }
    });
